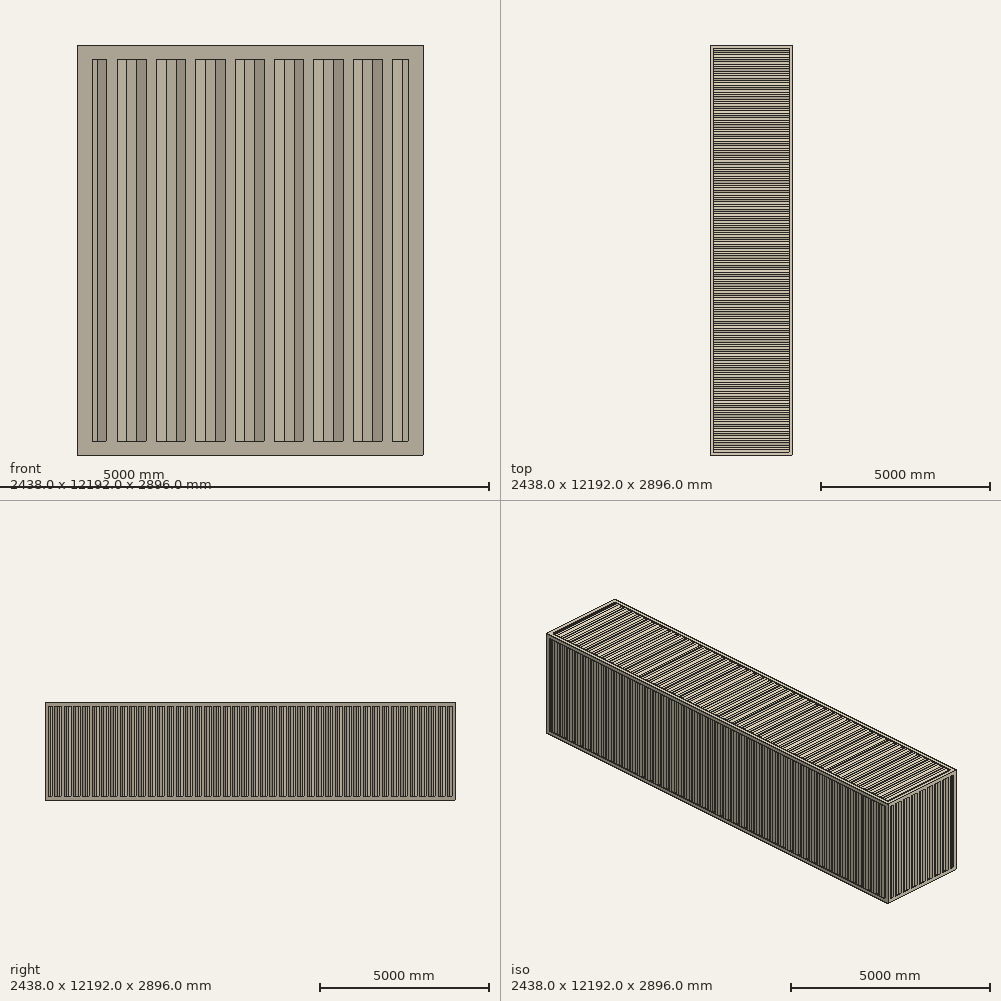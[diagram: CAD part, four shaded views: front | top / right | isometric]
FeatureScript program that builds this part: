
annotation { "Feature Type Name" : "Feature", "Feature Type Description" : "" }
export const myFeature = defineFeature(function(context is Context, id is Id, definition is map)
    precondition{}
    {
        {
            var Q0;
            Q0=qCreatedBy(makeId("Top.planeOp"),FACE);
            var sketch = newSketch(context, id + "F0", { "sketchPlane" : qUnion([Q0])});
            skLineSegment(sketch, "E0.bottom", {"start": v(0, 0) * mm, "end": v(-2438, 0) * mm});
            skLineSegment(sketch, "E0.top", {"start": v(0, 12192) * mm, "end": v(-2438, 12192) * mm});
            skLineSegment(sketch, "E0.left", {"start": v(0, 0) * mm, "end": v(0, 12192) * mm});
            skLineSegment(sketch, "E0.right", {"start": v(-2438, 0) * mm, "end": v(-2438, 12192) * mm});
            skSolve(sketch);
        }
        {
            var Q0;
            Q0=qSketchRegion(id+"F0",true);
            extrude(context, id + "F1", {"entities" : qUnion([Q0]), "depth" : 2896 * mm, "offsetDistance" : 25 * mm});
        }
        {
            var Q0;
            Q0=makeQuery(id+"F1.opExtrude","SWEPT_FACE",FACE,{"disambiguationData":[OSD([sQuery(id+"F0.wireOp",EDGE,"E0.bottom")])]});
            var sketch = newSketch(context, id + "F2", { "sketchPlane" : qUnion([Q0])});
            skLineSegment(sketch, "E1", {"start": v(-2438, 2896) * mm, "end": v(-2338, 2896) * mm});
            skLineSegment(sketch, "E2", {"start": v(-2338, 2896) * mm, "end": v(-2338, 100) * mm});
            skLineSegment(sketch, "E3", {"start": v(-2338, 100) * mm, "end": v(-100, 100) * mm});
            skLineSegment(sketch, "E4", {"start": v(-100, 100) * mm, "end": v(-100, 2796) * mm});
            skLineSegment(sketch, "E5", {"start": v(-100, 2796) * mm, "end": v(-2338, 2796) * mm});
            skSolve(sketch);
        }
        {
            var Q0;
            Q0=qSketchRegion(id+"F2",true);
            extrude(context, id + "F3", {"entities" : qUnion([Q0]), "operationType" : NewBodyOperationType.REMOVE, "oppositeDirection" : true, "depth" : 12192 * mm, "offsetDistance" : 25 * mm});
        }
        {
            var Q0;
            Q0=makeQuery(id+"F1.opExtrude","SWEPT_FACE",FACE,{"disambiguationData":[OSD([sQuery(id+"F0.wireOp",EDGE,"E0.left")])]});
            var sketch = newSketch(context, id + "F4", { "sketchPlane" : qUnion([Q0])});
            skLineSegment(sketch, "E6", {"start": v(0, 2896) * mm, "end": v(100, 2896) * mm});
            skLineSegment(sketch, "E7", {"start": v(100, 2896) * mm, "end": v(100, 100) * mm});
            skLineSegment(sketch, "E8", {"start": v(100, 100) * mm, "end": v(12092, 100) * mm});
            skLineSegment(sketch, "E9", {"start": v(12092, 100) * mm, "end": v(12092, 2796) * mm});
            skLineSegment(sketch, "E10", {"start": v(12092, 2796) * mm, "end": v(100, 2796) * mm});
            skSolve(sketch);
        }
        {
            var Q0;
            Q0=qSketchRegion(id+"F4",true);
            extrude(context, id + "F5", {"entities" : qUnion([Q0]), "operationType" : NewBodyOperationType.REMOVE, "oppositeDirection" : true, "depth" : 2438 * mm, "offsetDistance" : 25 * mm});
        }
        {
            var Q0;
            Q0=makeQuery(id+"F1.opExtrude","CAP_FACE",FACE,{"disambiguationData":[OSD([sQuery(id+"F0.wireOp",EDGE,"E0.bottom"),sQuery(id+"F0.wireOp",EDGE,"E0.top"),sQuery(id+"F0.wireOp",EDGE,"E0.left"),sQuery(id+"F0.wireOp",EDGE,"E0.right")])],"isStart":false});
            var sketch = newSketch(context, id + "F6", { "sketchPlane" : qUnion([Q0])});
            skLineSegment(sketch, "E11", {"start": v(-2438, 0) * mm, "end": v(-2338, 0) * mm});
            skLineSegment(sketch, "E12", {"start": v(-2338, 0) * mm, "end": v(-2338, 12092) * mm});
            skLineSegment(sketch, "E13", {"start": v(-2338, 12092) * mm, "end": v(-100, 12092) * mm});
            skLineSegment(sketch, "E14", {"start": v(-100, 12092) * mm, "end": v(-100, 100) * mm});
            skLineSegment(sketch, "E15", {"start": v(-100, 100) * mm, "end": v(-2338, 100) * mm});
            skSolve(sketch);
        }
        {
            var Q0;
            Q0=qSketchRegion(id+"F6",true);
            extrude(context, id + "F7", {"entities" : qUnion([Q0]), "operationType" : NewBodyOperationType.REMOVE, "oppositeDirection" : true, "depth" : 100 * mm, "offsetDistance" : 25 * mm});
        }
        {
            var Q0;
            Q0=makeQuery(id+"F5.boolean.opBoolean","MERGE",FACE,{"derivedFrom":[makeQuery(id+"F3.boolean.opBoolean","COPY",FACE,{"derivedFrom":makeQuery(id+"F3.opExtrude","SWEPT_FACE",FACE,{"disambiguationData":[OSD([sQuery(id+"F2.wireOp",EDGE,"E3")])]})})],"fromTools":[makeQuery(id+"F5.opExtrude","SWEPT_FACE",FACE,{"disambiguationData":[OSD([sQuery(id+"F4.wireOp",EDGE,"E8")])]})]});
            var sketch = newSketch(context, id + "F8", { "sketchPlane" : qUnion([Q0])});
            skLineSegment(sketch, "E16", {"start": v(-2338, 36) * mm, "end": v(-2301, 36) * mm});
            skLineSegment(sketch, "E17", {"start": v(-2233, 0) * mm, "end": v(-2161, 0) * mm});
            skLineSegment(sketch, "E18", {"start": v(-2093, 36) * mm, "end": v(-2023, 36) * mm});
            skLineSegment(sketch, "E19", {"start": v(-2301, 36) * mm, "end": v(-2233, 0) * mm});
            skLineSegment(sketch, "E20", {"start": v(-2161, 0) * mm, "end": v(-2093, 36) * mm});
            skLineSegment(sketch, "E21.1.0.0", {"start": v(-2023, 36) * mm, "end": v(-1955, 0) * mm});
            skLineSegment(sketch, "E21.1.0.1", {"start": v(-1955, 0) * mm, "end": v(-1883, 0) * mm});
            skLineSegment(sketch, "E21.1.0.2", {"start": v(-1883, 0) * mm, "end": v(-1815, 36) * mm});
            skLineSegment(sketch, "E21.1.0.3", {"start": v(-1815, 36) * mm, "end": v(-1745, 36) * mm});
            skLineSegment(sketch, "E21.2.0.0", {"start": v(-1745, 36) * mm, "end": v(-1677, 0) * mm});
            skLineSegment(sketch, "E21.2.0.1", {"start": v(-1677, 0) * mm, "end": v(-1605, 0) * mm});
            skLineSegment(sketch, "E21.2.0.2", {"start": v(-1605, 0) * mm, "end": v(-1537, 36) * mm});
            skLineSegment(sketch, "E21.2.0.3", {"start": v(-1537, 36) * mm, "end": v(-1467, 36) * mm});
            skLineSegment(sketch, "E21.3.0.0", {"start": v(-1467, 36) * mm, "end": v(-1399, 0) * mm});
            skLineSegment(sketch, "E21.3.0.1", {"start": v(-1399, 0) * mm, "end": v(-1327, 0) * mm});
            skLineSegment(sketch, "E21.3.0.2", {"start": v(-1327, 0) * mm, "end": v(-1259, 36) * mm});
            skLineSegment(sketch, "E21.3.0.3", {"start": v(-1259, 36) * mm, "end": v(-1189, 36) * mm});
            skLineSegment(sketch, "E21.4.0.0", {"start": v(-1189, 36) * mm, "end": v(-1121, 0) * mm});
            skLineSegment(sketch, "E21.4.0.1", {"start": v(-1121, 0) * mm, "end": v(-1049, 0) * mm});
            skLineSegment(sketch, "E21.4.0.2", {"start": v(-1049, 0) * mm, "end": v(-981, 36) * mm});
            skLineSegment(sketch, "E21.4.0.3", {"start": v(-981, 36) * mm, "end": v(-911, 36) * mm});
            skLineSegment(sketch, "E21.5.0.0", {"start": v(-911, 36) * mm, "end": v(-843, 0) * mm});
            skLineSegment(sketch, "E21.5.0.1", {"start": v(-843, 0) * mm, "end": v(-771, 0) * mm});
            skLineSegment(sketch, "E21.5.0.2", {"start": v(-771, 0) * mm, "end": v(-703, 36) * mm});
            skLineSegment(sketch, "E21.5.0.3", {"start": v(-703, 36) * mm, "end": v(-633, 36) * mm});
            skLineSegment(sketch, "E21.6.0.0", {"start": v(-633, 36) * mm, "end": v(-565, 0) * mm});
            skLineSegment(sketch, "E21.6.0.1", {"start": v(-565, 0) * mm, "end": v(-493, 0) * mm});
            skLineSegment(sketch, "E21.6.0.2", {"start": v(-493, 0) * mm, "end": v(-425, 36) * mm});
            skLineSegment(sketch, "E21.6.0.3", {"start": v(-425, 36) * mm, "end": v(-355, 36) * mm});
            skLineSegment(sketch, "E21.direction1", {"start": v(-2301, 36) * mm, "end": v(-2023, 36) * mm, "construction": true});
            skLineSegment(sketch, "E22.1.0.0", {"start": v(-355, 36) * mm, "end": v(-287, 0) * mm});
            skLineSegment(sketch, "E22.1.0.1", {"start": v(-287, 0) * mm, "end": v(-215, 0) * mm});
            skLineSegment(sketch, "E22.1.0.2", {"start": v(-215, 0) * mm, "end": v(-147, 36) * mm});
            skLineSegment(sketch, "E22.direction1", {"start": v(-633, 36) * mm, "end": v(-355, 36) * mm, "construction": true});
            skLineSegment(sketch, "E23", {"start": v(-147, 36) * mm, "end": v(-100, 36) * mm});
            skLineSegment(sketch, "E24.0.1.0", {"start": v(-2301, 37) * mm, "end": v(-2023, 37) * mm, "construction": true});
            skLineSegment(sketch, "E24.0.1.1", {"start": v(-633, 37) * mm, "end": v(-355, 37) * mm, "construction": true});
            skLineSegment(sketch, "E24.0.1.2", {"start": v(-355, 37) * mm, "end": v(-287, 1) * mm});
            skLineSegment(sketch, "E24.0.1.3", {"start": v(-1259, 37) * mm, "end": v(-1189, 37) * mm});
            skLineSegment(sketch, "E24.0.1.4", {"start": v(-147, 37) * mm, "end": v(-100, 37) * mm});
            skLineSegment(sketch, "E24.0.1.5", {"start": v(-1605, 1) * mm, "end": v(-1537, 37) * mm});
            skLineSegment(sketch, "E24.0.1.6", {"start": v(-1467, 37) * mm, "end": v(-1399, 1) * mm});
            skLineSegment(sketch, "E24.0.1.7", {"start": v(-1049, 1) * mm, "end": v(-981, 37) * mm});
            skLineSegment(sketch, "E24.0.1.8", {"start": v(-633, 37) * mm, "end": v(-565, 1) * mm});
            skLineSegment(sketch, "E24.0.1.9", {"start": v(-1955, 1) * mm, "end": v(-1883, 1) * mm});
            skLineSegment(sketch, "E24.0.1.10", {"start": v(-215, 1) * mm, "end": v(-147, 37) * mm});
            skLineSegment(sketch, "E24.0.1.11", {"start": v(-911, 37) * mm, "end": v(-843, 1) * mm});
            skLineSegment(sketch, "E24.0.1.12", {"start": v(-1883, 1) * mm, "end": v(-1815, 37) * mm});
            skLineSegment(sketch, "E24.0.1.13", {"start": v(-2023, 37) * mm, "end": v(-1955, 1) * mm});
            skLineSegment(sketch, "E24.0.1.14", {"start": v(-493, 1) * mm, "end": v(-425, 37) * mm});
            skLineSegment(sketch, "E24.0.1.15", {"start": v(-1677, 1) * mm, "end": v(-1605, 1) * mm});
            skLineSegment(sketch, "E24.0.1.16", {"start": v(-1189, 37) * mm, "end": v(-1121, 1) * mm});
            skLineSegment(sketch, "E24.0.1.17", {"start": v(-1745, 37) * mm, "end": v(-1677, 1) * mm});
            skLineSegment(sketch, "E24.0.1.18", {"start": v(-287, 1) * mm, "end": v(-215, 1) * mm});
            skLineSegment(sketch, "E24.0.1.19", {"start": v(-981, 37) * mm, "end": v(-911, 37) * mm});
            skLineSegment(sketch, "E24.0.1.20", {"start": v(-843, 1) * mm, "end": v(-771, 1) * mm});
            skLineSegment(sketch, "E24.0.1.21", {"start": v(-771, 1) * mm, "end": v(-703, 37) * mm});
            skLineSegment(sketch, "E24.0.1.22", {"start": v(-1815, 37) * mm, "end": v(-1745, 37) * mm});
            skLineSegment(sketch, "E24.0.1.23", {"start": v(-565, 1) * mm, "end": v(-493, 1) * mm});
            skLineSegment(sketch, "E24.0.1.24", {"start": v(-2161, 1) * mm, "end": v(-2093, 37) * mm});
            skLineSegment(sketch, "E24.0.1.25", {"start": v(-1121, 1) * mm, "end": v(-1049, 1) * mm});
            skLineSegment(sketch, "E24.0.1.26", {"start": v(-2301, 37) * mm, "end": v(-2233, 1) * mm});
            skLineSegment(sketch, "E24.0.1.27", {"start": v(-1537, 37) * mm, "end": v(-1467, 37) * mm});
            skLineSegment(sketch, "E24.0.1.28", {"start": v(-1399, 1) * mm, "end": v(-1327, 1) * mm});
            skLineSegment(sketch, "E24.0.1.29", {"start": v(-2233, 1) * mm, "end": v(-2161, 1) * mm});
            skLineSegment(sketch, "E24.0.1.30", {"start": v(-1327, 1) * mm, "end": v(-1259, 37) * mm});
            skLineSegment(sketch, "E24.0.1.31", {"start": v(-425, 37) * mm, "end": v(-355, 37) * mm});
            skLineSegment(sketch, "E24.0.1.32", {"start": v(-2093, 37) * mm, "end": v(-2023, 37) * mm});
            skLineSegment(sketch, "E24.0.1.33", {"start": v(-703, 37) * mm, "end": v(-633, 37) * mm});
            skLineSegment(sketch, "E24.0.1.34", {"start": v(-2338, 37) * mm, "end": v(-2301, 37) * mm});
            skLineSegment(sketch, "E24.direction1", {"start": v(-2338, 36) * mm, "end": v(-2313, 36) * mm, "construction": true});
            skLineSegment(sketch, "E24.direction2", {"start": v(-2338, 36) * mm, "end": v(-2338, 37) * mm, "construction": true});
            skLineSegment(sketch, "E25", {"start": v(-2338, 37) * mm, "end": v(-2338, 36) * mm});
            skLineSegment(sketch, "E26", {"start": v(-100, 37) * mm, "end": v(-100, 36) * mm});
            skSolve(sketch);
        }
        {
            var Q0;
            Q0=qSketchRegion(id+"F8",true);
            extrude(context, id + "F9", {"entities" : qUnion([Q0]), "operationType" : NewBodyOperationType.ADD, "depth" : 2696 * mm, "offsetDistance" : 25 * mm});
        }
        {
            var Q0;
            {var subQ4=makeQuery(id+"F3.boolean.opBoolean","COPY",FACE,{"derivedFrom":makeQuery(id+"F3.opExtrude","SWEPT_FACE",FACE,{"disambiguationData":[OSD([sQuery(id+"F2.wireOp",EDGE,"E3")])]})});var subQ5=makeQuery(id+"F5.opExtrude","SWEPT_FACE",FACE,{"disambiguationData":[OSD([sQuery(id+"F4.wireOp",EDGE,"E8")])]});Q0=makeQuery(id+"F9.boolean.opBoolean","SPLIT",FACE,{"disambiguationData":[TD([makeQuery(id+"F1.opExtrude","SWEPT_FACE",FACE,{"disambiguationData":[OSD([sQuery(id+"F0.wireOp",EDGE,"E0.top")])]})])],"derivedFrom":makeQuery(id+"F5.boolean.opBoolean","MERGE",FACE,{"derivedFrom":[subQ4],"fromTools":[subQ5]})});}
            var sketch = newSketch(context, id + "F10", { "sketchPlane" : qUnion([Q0])});
            skLineSegment(sketch, "E27", {"start": v(-100, 12156) * mm, "end": v(-137, 12156) * mm});
            skLineSegment(sketch, "E28", {"start": v(-205.08, 12191.96) * mm, "end": v(-277.08, 12191.96) * mm});
            skLineSegment(sketch, "E29", {"start": v(-345, 12156) * mm, "end": v(-415, 12156) * mm});
            skLineSegment(sketch, "E30", {"start": v(-137, 12156) * mm, "end": v(-205.08, 12191.96) * mm});
            skLineSegment(sketch, "E31", {"start": v(-277.08, 12191.96) * mm, "end": v(-345, 12156) * mm});
            skLineSegment(sketch, "E32.1.0.0", {"start": v(-415, 12156) * mm, "end": v(-483.08, 12191.96) * mm});
            skLineSegment(sketch, "E32.1.0.1", {"start": v(-483.08, 12191.96) * mm, "end": v(-555.08, 12191.96) * mm});
            skLineSegment(sketch, "E32.1.0.2", {"start": v(-555.08, 12191.96) * mm, "end": v(-623, 12156) * mm});
            skLineSegment(sketch, "E32.1.0.3", {"start": v(-623, 12156) * mm, "end": v(-693, 12156) * mm});
            skLineSegment(sketch, "E32.2.0.0", {"start": v(-693, 12156) * mm, "end": v(-761.08, 12191.96) * mm});
            skLineSegment(sketch, "E32.2.0.1", {"start": v(-761.08, 12191.96) * mm, "end": v(-833.08, 12191.96) * mm});
            skLineSegment(sketch, "E32.2.0.2", {"start": v(-833.08, 12191.96) * mm, "end": v(-901, 12156) * mm});
            skLineSegment(sketch, "E32.2.0.3", {"start": v(-901, 12156) * mm, "end": v(-971, 12156) * mm});
            skLineSegment(sketch, "E32.3.0.0", {"start": v(-971, 12156) * mm, "end": v(-1039.08, 12191.96) * mm});
            skLineSegment(sketch, "E32.3.0.1", {"start": v(-1039.08, 12191.96) * mm, "end": v(-1111.08, 12191.96) * mm});
            skLineSegment(sketch, "E32.3.0.2", {"start": v(-1111.08, 12191.96) * mm, "end": v(-1179, 12156) * mm});
            skLineSegment(sketch, "E32.3.0.3", {"start": v(-1179, 12156) * mm, "end": v(-1249, 12156) * mm});
            skLineSegment(sketch, "E32.4.0.0", {"start": v(-1249, 12156) * mm, "end": v(-1317.08, 12191.96) * mm});
            skLineSegment(sketch, "E32.4.0.1", {"start": v(-1317.08, 12191.96) * mm, "end": v(-1389.08, 12191.96) * mm});
            skLineSegment(sketch, "E32.4.0.2", {"start": v(-1389.08, 12191.96) * mm, "end": v(-1457, 12156) * mm});
            skLineSegment(sketch, "E32.4.0.3", {"start": v(-1457, 12156) * mm, "end": v(-1527, 12156) * mm});
            skLineSegment(sketch, "E32.5.0.0", {"start": v(-1527, 12156) * mm, "end": v(-1595.08, 12191.96) * mm});
            skLineSegment(sketch, "E32.5.0.1", {"start": v(-1595.08, 12191.96) * mm, "end": v(-1667.08, 12191.96) * mm});
            skLineSegment(sketch, "E32.5.0.2", {"start": v(-1667.08, 12191.96) * mm, "end": v(-1735, 12156) * mm});
            skLineSegment(sketch, "E32.5.0.3", {"start": v(-1735, 12156) * mm, "end": v(-1805, 12156) * mm});
            skLineSegment(sketch, "E32.6.0.0", {"start": v(-1805, 12156) * mm, "end": v(-1873.08, 12191.96) * mm});
            skLineSegment(sketch, "E32.6.0.1", {"start": v(-1873.08, 12191.96) * mm, "end": v(-1945.08, 12191.96) * mm});
            skLineSegment(sketch, "E32.6.0.2", {"start": v(-1945.08, 12191.96) * mm, "end": v(-2013, 12156) * mm});
            skLineSegment(sketch, "E32.6.0.3", {"start": v(-2013, 12156) * mm, "end": v(-2083, 12156) * mm});
            skLineSegment(sketch, "E32.direction1", {"start": v(-137, 12156) * mm, "end": v(-415, 12156) * mm, "construction": true});
            skLineSegment(sketch, "E33.1.0.0", {"start": v(-2083, 12156) * mm, "end": v(-2151.08, 12191.96) * mm});
            skLineSegment(sketch, "E33.1.0.1", {"start": v(-2151.08, 12191.96) * mm, "end": v(-2223.08, 12191.96) * mm});
            skLineSegment(sketch, "E33.1.0.2", {"start": v(-2223.08, 12191.96) * mm, "end": v(-2291, 12156) * mm});
            skLineSegment(sketch, "E33.direction1", {"start": v(-1805, 12156) * mm, "end": v(-2083, 12156) * mm, "construction": true});
            skLineSegment(sketch, "E34", {"start": v(-2291, 12156) * mm, "end": v(-2338, 12156) * mm});
            skLineSegment(sketch, "E35.0.1.0", {"start": v(-137, 12155) * mm, "end": v(-415, 12155) * mm, "construction": true});
            skLineSegment(sketch, "E35.0.1.1", {"start": v(-1805, 12155) * mm, "end": v(-2083, 12155) * mm, "construction": true});
            skLineSegment(sketch, "E35.0.1.2", {"start": v(-2083, 12155) * mm, "end": v(-2151.08, 12190.96) * mm});
            skLineSegment(sketch, "E35.0.1.3", {"start": v(-1179, 12155) * mm, "end": v(-1249, 12155) * mm});
            skLineSegment(sketch, "E35.0.1.4", {"start": v(-2291, 12155) * mm, "end": v(-2338, 12155) * mm});
            skLineSegment(sketch, "E35.0.1.5", {"start": v(-833.08, 12190.96) * mm, "end": v(-901, 12155) * mm});
            skLineSegment(sketch, "E35.0.1.6", {"start": v(-971, 12155) * mm, "end": v(-1039.08, 12190.96) * mm});
            skLineSegment(sketch, "E35.0.1.7", {"start": v(-1389.08, 12190.96) * mm, "end": v(-1457, 12155) * mm});
            skLineSegment(sketch, "E35.0.1.8", {"start": v(-1805, 12155) * mm, "end": v(-1873.08, 12190.96) * mm});
            skLineSegment(sketch, "E35.0.1.9", {"start": v(-483.08, 12190.96) * mm, "end": v(-555.08, 12190.96) * mm});
            skLineSegment(sketch, "E35.0.1.10", {"start": v(-2223.08, 12190.96) * mm, "end": v(-2291, 12155) * mm});
            skLineSegment(sketch, "E35.0.1.11", {"start": v(-1527, 12155) * mm, "end": v(-1595.08, 12190.96) * mm});
            skLineSegment(sketch, "E35.0.1.12", {"start": v(-555.08, 12190.96) * mm, "end": v(-623, 12155) * mm});
            skLineSegment(sketch, "E35.0.1.13", {"start": v(-415, 12155) * mm, "end": v(-483.08, 12190.96) * mm});
            skLineSegment(sketch, "E35.0.1.14", {"start": v(-1945.08, 12190.96) * mm, "end": v(-2013, 12155) * mm});
            skLineSegment(sketch, "E35.0.1.15", {"start": v(-761.08, 12190.96) * mm, "end": v(-833.08, 12190.96) * mm});
            skLineSegment(sketch, "E35.0.1.16", {"start": v(-1249, 12155) * mm, "end": v(-1317.08, 12190.96) * mm});
            skLineSegment(sketch, "E35.0.1.17", {"start": v(-693, 12155) * mm, "end": v(-761.08, 12190.96) * mm});
            skLineSegment(sketch, "E35.0.1.18", {"start": v(-2151.08, 12190.96) * mm, "end": v(-2223.08, 12190.96) * mm});
            skLineSegment(sketch, "E35.0.1.19", {"start": v(-1457, 12155) * mm, "end": v(-1527, 12155) * mm});
            skLineSegment(sketch, "E35.0.1.20", {"start": v(-1595.08, 12190.96) * mm, "end": v(-1667.08, 12190.96) * mm});
            skLineSegment(sketch, "E35.0.1.21", {"start": v(-1667.08, 12190.96) * mm, "end": v(-1735, 12155) * mm});
            skLineSegment(sketch, "E35.0.1.22", {"start": v(-623, 12155) * mm, "end": v(-693, 12155) * mm});
            skLineSegment(sketch, "E35.0.1.23", {"start": v(-1873.08, 12190.96) * mm, "end": v(-1945.08, 12190.96) * mm});
            skLineSegment(sketch, "E35.0.1.24", {"start": v(-277.08, 12190.96) * mm, "end": v(-345, 12155) * mm});
            skLineSegment(sketch, "E35.0.1.25", {"start": v(-1317.08, 12190.96) * mm, "end": v(-1389.08, 12190.96) * mm});
            skLineSegment(sketch, "E35.0.1.26", {"start": v(-137, 12155) * mm, "end": v(-205.08, 12190.96) * mm});
            skLineSegment(sketch, "E35.0.1.27", {"start": v(-901, 12155) * mm, "end": v(-971, 12155) * mm});
            skLineSegment(sketch, "E35.0.1.28", {"start": v(-1039.08, 12190.96) * mm, "end": v(-1111.08, 12190.96) * mm});
            skLineSegment(sketch, "E35.0.1.29", {"start": v(-205.08, 12190.96) * mm, "end": v(-277.08, 12190.96) * mm});
            skLineSegment(sketch, "E35.0.1.30", {"start": v(-1111.08, 12190.96) * mm, "end": v(-1179, 12155) * mm});
            skLineSegment(sketch, "E35.0.1.31", {"start": v(-2013, 12155) * mm, "end": v(-2083, 12155) * mm});
            skLineSegment(sketch, "E35.0.1.32", {"start": v(-345, 12155) * mm, "end": v(-415, 12155) * mm});
            skLineSegment(sketch, "E35.0.1.33", {"start": v(-1735, 12155) * mm, "end": v(-1805, 12155) * mm});
            skLineSegment(sketch, "E35.0.1.34", {"start": v(-100, 12155) * mm, "end": v(-137, 12155) * mm});
            skLineSegment(sketch, "E35.direction1", {"start": v(-100, 12156) * mm, "end": v(-125, 12156) * mm, "construction": true});
            skLineSegment(sketch, "E35.direction2", {"start": v(-100, 12156) * mm, "end": v(-100, 12155) * mm, "construction": true});
            skLineSegment(sketch, "E36", {"start": v(-100, 12156) * mm, "end": v(-100, 12155) * mm});
            skLineSegment(sketch, "E37", {"start": v(-2338, 12156) * mm, "end": v(-2338, 12155) * mm});
            skSolve(sketch);
        }
        {
            var Q0;
            Q0=qSketchRegion(id+"F10",true);
            extrude(context, id + "F11", {"entities" : qUnion([Q0]), "operationType" : NewBodyOperationType.ADD, "depth" : 2696 * mm, "offsetDistance" : 25 * mm});
        }
        {
            var Q0;
            {var subQ5=makeQuery(id+"F3.boolean.opBoolean","COPY",FACE,{"derivedFrom":makeQuery(id+"F3.opExtrude","SWEPT_FACE",FACE,{"disambiguationData":[OSD([sQuery(id+"F2.wireOp",EDGE,"E3")])]})});var subQ6=makeQuery(id+"F5.opExtrude","SWEPT_FACE",FACE,{"disambiguationData":[OSD([sQuery(id+"F4.wireOp",EDGE,"E8")])]});var subQ12=makeQuery(id+"F1.opExtrude","SWEPT_FACE",FACE,{"disambiguationData":[OSD([sQuery(id+"F0.wireOp",EDGE,"E0.left")])]});Q0=makeQuery(id+"F11.boolean.opBoolean","SPLIT",FACE,{"disambiguationData":[TD([subQ12])],"derivedFrom":makeQuery(id+"F9.boolean.opBoolean","SPLIT",FACE,{"disambiguationData":[TD([makeQuery(id+"F1.opExtrude","SWEPT_FACE",FACE,{"disambiguationData":[OSD([sQuery(id+"F0.wireOp",EDGE,"E0.top")])]})])],"derivedFrom":makeQuery(id+"F5.boolean.opBoolean","MERGE",FACE,{"derivedFrom":[subQ5],"fromTools":[subQ6]})})});}
            var sketch = newSketch(context, id + "F12", { "sketchPlane" : qUnion([Q0])});
            skLineSegment(sketch, "E38", {"start": v(0, 100) * mm, "end": v(-36, 100) * mm});
            skLineSegment(sketch, "E39", {"start": v(-36, 100.17) * mm, "end": v(-36, 137.17) * mm});
            skLineSegment(sketch, "E40", {"start": v(0, 205.17) * mm, "end": v(0, 277.17) * mm});
            skLineSegment(sketch, "E41", {"start": v(-36, 345.17) * mm, "end": v(-36, 415.17) * mm});
            skLineSegment(sketch, "E42", {"start": v(-36, 137.17) * mm, "end": v(0, 205.17) * mm});
            skLineSegment(sketch, "E43", {"start": v(0, 277.17) * mm, "end": v(-36, 345.17) * mm});
            skLineSegment(sketch, "E44.1.0.0", {"start": v(-36, 415.17) * mm, "end": v(0, 483.17) * mm});
            skLineSegment(sketch, "E44.1.0.1", {"start": v(0, 483.17) * mm, "end": v(0, 555.17) * mm});
            skLineSegment(sketch, "E44.1.0.2", {"start": v(0, 555.17) * mm, "end": v(-36, 623.17) * mm});
            skLineSegment(sketch, "E44.1.0.3", {"start": v(-36, 623.17) * mm, "end": v(-36, 693.17) * mm});
            skLineSegment(sketch, "E44.2.0.0", {"start": v(-36, 693.17) * mm, "end": v(0, 761.17) * mm});
            skLineSegment(sketch, "E44.2.0.1", {"start": v(0, 761.17) * mm, "end": v(0, 833.17) * mm});
            skLineSegment(sketch, "E44.2.0.2", {"start": v(0, 833.17) * mm, "end": v(-36, 901.17) * mm});
            skLineSegment(sketch, "E44.2.0.3", {"start": v(-36, 901.17) * mm, "end": v(-36, 971.17) * mm});
            skLineSegment(sketch, "E44.3.0.0", {"start": v(-36, 971.17) * mm, "end": v(0, 1039.17) * mm});
            skLineSegment(sketch, "E44.3.0.1", {"start": v(0, 1039.17) * mm, "end": v(0, 1111.17) * mm});
            skLineSegment(sketch, "E44.3.0.2", {"start": v(0, 1111.17) * mm, "end": v(-36, 1179.17) * mm});
            skLineSegment(sketch, "E44.3.0.3", {"start": v(-36, 1179.17) * mm, "end": v(-36, 1249.17) * mm});
            skLineSegment(sketch, "E44.4.0.0", {"start": v(-36, 1249.17) * mm, "end": v(0, 1317.17) * mm});
            skLineSegment(sketch, "E44.4.0.1", {"start": v(0, 1317.17) * mm, "end": v(0, 1389.17) * mm});
            skLineSegment(sketch, "E44.4.0.2", {"start": v(0, 1389.17) * mm, "end": v(-36, 1457.17) * mm});
            skLineSegment(sketch, "E44.4.0.3", {"start": v(-36, 1457.17) * mm, "end": v(-36, 1527.17) * mm});
            skLineSegment(sketch, "E44.5.0.0", {"start": v(-36, 1527.17) * mm, "end": v(0, 1595.17) * mm});
            skLineSegment(sketch, "E44.5.0.1", {"start": v(0, 1595.17) * mm, "end": v(0, 1667.17) * mm});
            skLineSegment(sketch, "E44.5.0.2", {"start": v(0, 1667.17) * mm, "end": v(-36, 1735.17) * mm});
            skLineSegment(sketch, "E44.5.0.3", {"start": v(-36, 1735.17) * mm, "end": v(-36, 1805.17) * mm});
            skLineSegment(sketch, "E44.6.0.0", {"start": v(-36, 1805.17) * mm, "end": v(0, 1873.17) * mm});
            skLineSegment(sketch, "E44.6.0.1", {"start": v(0, 1873.17) * mm, "end": v(0, 1945.17) * mm});
            skLineSegment(sketch, "E44.6.0.2", {"start": v(0, 1945.17) * mm, "end": v(-36, 2013.17) * mm});
            skLineSegment(sketch, "E44.6.0.3", {"start": v(-36, 2013.17) * mm, "end": v(-36, 2083.17) * mm});
            skLineSegment(sketch, "E44.direction1", {"start": v(-36, 137.17) * mm, "end": v(-36, 415.17) * mm, "construction": true});
            skLineSegment(sketch, "E45.1.0.0", {"start": v(-36, 2083.17) * mm, "end": v(0, 2151.17) * mm});
            skLineSegment(sketch, "E45.1.0.1", {"start": v(0, 2151.17) * mm, "end": v(0, 2223.17) * mm});
            skLineSegment(sketch, "E45.1.0.2", {"start": v(0, 2223.17) * mm, "end": v(-36, 2291.17) * mm});
            skLineSegment(sketch, "E45.direction1", {"start": v(-36, 1805.17) * mm, "end": v(-36, 2083.17) * mm, "construction": true});
            skLineSegment(sketch, "E46.0.1.0", {"start": v(-37, 137.17) * mm, "end": v(-37, 415.17) * mm, "construction": true});
            skLineSegment(sketch, "E46.0.1.1", {"start": v(-37, 1805.17) * mm, "end": v(-37, 2083.17) * mm, "construction": true});
            skLineSegment(sketch, "E46.0.1.2", {"start": v(-37, 2083.17) * mm, "end": v(-1, 2151.17) * mm});
            skLineSegment(sketch, "E46.0.1.3", {"start": v(-37, 1179.17) * mm, "end": v(-37, 1249.17) * mm});
            skLineSegment(sketch, "E46.0.1.5", {"start": v(-1, 833.17) * mm, "end": v(-37, 901.17) * mm});
            skLineSegment(sketch, "E46.0.1.6", {"start": v(-37, 971.17) * mm, "end": v(-1, 1039.17) * mm});
            skLineSegment(sketch, "E46.0.1.7", {"start": v(-1, 1389.17) * mm, "end": v(-37, 1457.17) * mm});
            skLineSegment(sketch, "E46.0.1.8", {"start": v(-37, 1805.17) * mm, "end": v(-1, 1873.17) * mm});
            skLineSegment(sketch, "E46.0.1.9", {"start": v(-1, 483.17) * mm, "end": v(-1, 555.17) * mm});
            skLineSegment(sketch, "E46.0.1.10", {"start": v(-1, 2223.17) * mm, "end": v(-37, 2291.17) * mm});
            skLineSegment(sketch, "E46.0.1.11", {"start": v(-37, 1527.17) * mm, "end": v(-1, 1595.17) * mm});
            skLineSegment(sketch, "E46.0.1.12", {"start": v(-1, 555.17) * mm, "end": v(-37, 623.17) * mm});
            skLineSegment(sketch, "E46.0.1.13", {"start": v(-37, 415.17) * mm, "end": v(-1, 483.17) * mm});
            skLineSegment(sketch, "E46.0.1.14", {"start": v(-1, 1945.17) * mm, "end": v(-37, 2013.17) * mm});
            skLineSegment(sketch, "E46.0.1.15", {"start": v(-1, 761.17) * mm, "end": v(-1, 833.17) * mm});
            skLineSegment(sketch, "E46.0.1.16", {"start": v(-37, 1249.17) * mm, "end": v(-1, 1317.17) * mm});
            skLineSegment(sketch, "E46.0.1.17", {"start": v(-37, 693.17) * mm, "end": v(-1, 761.17) * mm});
            skLineSegment(sketch, "E46.0.1.18", {"start": v(-1, 2151.17) * mm, "end": v(-1, 2223.17) * mm});
            skLineSegment(sketch, "E46.0.1.19", {"start": v(-37, 1457.17) * mm, "end": v(-37, 1527.17) * mm});
            skLineSegment(sketch, "E46.0.1.20", {"start": v(-1, 1595.17) * mm, "end": v(-1, 1667.17) * mm});
            skLineSegment(sketch, "E46.0.1.21", {"start": v(-1, 1667.17) * mm, "end": v(-37, 1735.17) * mm});
            skLineSegment(sketch, "E46.0.1.22", {"start": v(-37, 623.17) * mm, "end": v(-37, 693.17) * mm});
            skLineSegment(sketch, "E46.0.1.23", {"start": v(-1, 1873.17) * mm, "end": v(-1, 1945.17) * mm});
            skLineSegment(sketch, "E46.0.1.24", {"start": v(-1, 277.17) * mm, "end": v(-37, 345.17) * mm});
            skLineSegment(sketch, "E46.0.1.25", {"start": v(-1, 1317.17) * mm, "end": v(-1, 1389.17) * mm});
            skLineSegment(sketch, "E46.0.1.26", {"start": v(-37, 137.17) * mm, "end": v(-1, 205.17) * mm});
            skLineSegment(sketch, "E46.0.1.27", {"start": v(-37, 901.17) * mm, "end": v(-37, 971.17) * mm});
            skLineSegment(sketch, "E46.0.1.28", {"start": v(-1, 1039.17) * mm, "end": v(-1, 1111.17) * mm});
            skLineSegment(sketch, "E46.0.1.29", {"start": v(-1, 205.17) * mm, "end": v(-1, 277.17) * mm});
            skLineSegment(sketch, "E46.0.1.30", {"start": v(-1, 1111.17) * mm, "end": v(-37, 1179.17) * mm});
            skLineSegment(sketch, "E46.0.1.31", {"start": v(-37, 2013.17) * mm, "end": v(-37, 2083.17) * mm});
            skLineSegment(sketch, "E46.0.1.32", {"start": v(-37, 345.17) * mm, "end": v(-37, 415.17) * mm});
            skLineSegment(sketch, "E46.0.1.33", {"start": v(-37, 1735.17) * mm, "end": v(-37, 1805.17) * mm});
            skLineSegment(sketch, "E46.0.1.34", {"start": v(-37, 100.17) * mm, "end": v(-37, 137.17) * mm});
            skLineSegment(sketch, "E47", {"start": v(-37, 100.17) * mm, "end": v(-37, 100) * mm});
            skLineSegment(sketch, "E48", {"start": v(-37, 100) * mm, "end": v(-36, 100) * mm});
            skLineSegment(sketch, "E49", {"start": v(-36, 100) * mm, "end": v(-36, 100.17) * mm});
            skLineSegment(sketch, "E50.0.1.0", {"start": v(0, 2779.17) * mm, "end": v(-36, 2847.17) * mm});
            skLineSegment(sketch, "E50.0.1.1", {"start": v(-1, 2779.17) * mm, "end": v(-37, 2847.17) * mm});
            skLineSegment(sketch, "E50.0.1.2", {"start": v(0, 2707.17) * mm, "end": v(0, 2779.17) * mm});
            skLineSegment(sketch, "E50.0.1.3", {"start": v(0, 2429.17) * mm, "end": v(0, 2501.17) * mm});
            skLineSegment(sketch, "E50.0.1.4", {"start": v(-37, 2639.17) * mm, "end": v(-1, 2707.17) * mm});
            skLineSegment(sketch, "E50.0.1.5", {"start": v(-37, 2569.17) * mm, "end": v(-37, 2639.17) * mm});
            skLineSegment(sketch, "E50.0.1.6", {"start": v(-37, 2917.17) * mm, "end": v(-1, 2985.17) * mm});
            skLineSegment(sketch, "E50.0.1.7", {"start": v(-1, 2501.17) * mm, "end": v(-37, 2569.17) * mm});
            skLineSegment(sketch, "E50.0.1.8", {"start": v(-36, 2917.17) * mm, "end": v(0, 2985.17) * mm});
            skLineSegment(sketch, "E50.0.1.9", {"start": v(-36, 2569.17) * mm, "end": v(-36, 2639.17) * mm});
            skLineSegment(sketch, "E50.0.1.10", {"start": v(-37, 2291.17) * mm, "end": v(-37, 2361.17) * mm});
            skLineSegment(sketch, "E50.0.1.11", {"start": v(-36, 2847.17) * mm, "end": v(-36, 2917.17) * mm});
            skLineSegment(sketch, "E50.0.1.12", {"start": v(-1, 2707.17) * mm, "end": v(-1, 2779.17) * mm});
            skLineSegment(sketch, "E50.0.1.13", {"start": v(-37, 2361.17) * mm, "end": v(-1, 2429.17) * mm});
            skLineSegment(sketch, "E50.0.1.14", {"start": v(-36, 2361.17) * mm, "end": v(0, 2429.17) * mm});
            skLineSegment(sketch, "E50.0.1.15", {"start": v(0, 2985.17) * mm, "end": v(0, 3057.17) * mm});
            skLineSegment(sketch, "E50.0.1.16", {"start": v(0, 2501.17) * mm, "end": v(-36, 2569.17) * mm});
            skLineSegment(sketch, "E50.0.1.17", {"start": v(-36, 2291.17) * mm, "end": v(-36, 2361.17) * mm});
            skLineSegment(sketch, "E50.0.1.18", {"start": v(-1, 2429.17) * mm, "end": v(-1, 2501.17) * mm});
            skLineSegment(sketch, "E50.0.1.19", {"start": v(-36, 2639.17) * mm, "end": v(0, 2707.17) * mm});
            skLineSegment(sketch, "E50.0.1.20", {"start": v(-1, 2985.17) * mm, "end": v(-1, 3057.17) * mm});
            skLineSegment(sketch, "E50.0.1.21", {"start": v(-37, 2847.17) * mm, "end": v(-37, 2917.17) * mm});
            skLineSegment(sketch, "E50.0.1.22", {"start": v(-36, 3751.17) * mm, "end": v(-36, 4029.17) * mm, "construction": true});
            skLineSegment(sketch, "E50.0.1.23", {"start": v(0, 4169.17) * mm, "end": v(-36, 4237.17) * mm});
            skLineSegment(sketch, "E50.0.1.24", {"start": v(-1, 4169.17) * mm, "end": v(-37, 4237.17) * mm});
            skLineSegment(sketch, "E50.0.1.25", {"start": v(-37, 3751.17) * mm, "end": v(-37, 4029.17) * mm, "construction": true});
            skLineSegment(sketch, "E50.0.1.26", {"start": v(-1, 3335.17) * mm, "end": v(-37, 3403.17) * mm});
            skLineSegment(sketch, "E50.0.1.27", {"start": v(0, 3335.17) * mm, "end": v(-36, 3403.17) * mm});
            skLineSegment(sketch, "E50.0.1.28", {"start": v(0, 4097.17) * mm, "end": v(0, 4169.17) * mm});
            skLineSegment(sketch, "E50.0.1.29", {"start": v(-36, 4029.17) * mm, "end": v(0, 4097.17) * mm});
            skLineSegment(sketch, "E50.0.1.30", {"start": v(0, 3263.17) * mm, "end": v(0, 3335.17) * mm});
            skLineSegment(sketch, "E50.0.1.31", {"start": v(-1, 3263.17) * mm, "end": v(-1, 3335.17) * mm});
            skLineSegment(sketch, "E50.0.1.32", {"start": v(-37, 4029.17) * mm, "end": v(-1, 4097.17) * mm});
            skLineSegment(sketch, "E50.0.1.33", {"start": v(-1, 4097.17) * mm, "end": v(-1, 4169.17) * mm});
            skLineSegment(sketch, "E50.0.1.34", {"start": v(-37, 3681.17) * mm, "end": v(-37, 3751.17) * mm});
            skLineSegment(sketch, "E50.0.1.35", {"start": v(-1, 3541.17) * mm, "end": v(-1, 3613.17) * mm});
            skLineSegment(sketch, "E50.0.1.36", {"start": v(-37, 3125.17) * mm, "end": v(-37, 3195.17) * mm});
            skLineSegment(sketch, "E50.0.1.37", {"start": v(-1, 3891.17) * mm, "end": v(-37, 3959.17) * mm});
            skLineSegment(sketch, "E50.0.1.38", {"start": v(-36, 3473.17) * mm, "end": v(0, 3541.17) * mm});
            skLineSegment(sketch, "E50.0.1.39", {"start": v(-1, 3613.17) * mm, "end": v(-37, 3681.17) * mm});
            skLineSegment(sketch, "E50.0.1.40", {"start": v(0, 3819.17) * mm, "end": v(0, 3891.17) * mm});
            skLineSegment(sketch, "E50.0.1.41", {"start": v(-36, 3751.17) * mm, "end": v(0, 3819.17) * mm});
            skLineSegment(sketch, "E50.0.1.42", {"start": v(0, 3541.17) * mm, "end": v(0, 3613.17) * mm});
            skLineSegment(sketch, "E50.0.1.43", {"start": v(-36, 3125.17) * mm, "end": v(-36, 3195.17) * mm});
            skLineSegment(sketch, "E50.0.1.44", {"start": v(-37, 3473.17) * mm, "end": v(-1, 3541.17) * mm});
            skLineSegment(sketch, "E50.0.1.45", {"start": v(-37, 3195.17) * mm, "end": v(-1, 3263.17) * mm});
            skLineSegment(sketch, "E50.0.1.46", {"start": v(-1, 3057.17) * mm, "end": v(-37, 3125.17) * mm});
            skLineSegment(sketch, "E50.0.1.47", {"start": v(-1, 3819.17) * mm, "end": v(-1, 3891.17) * mm});
            skLineSegment(sketch, "E50.0.1.48", {"start": v(-37, 3403.17) * mm, "end": v(-37, 3473.17) * mm});
            skLineSegment(sketch, "E50.0.1.49", {"start": v(-37, 3959.17) * mm, "end": v(-37, 4029.17) * mm});
            skLineSegment(sketch, "E50.0.1.50", {"start": v(-36, 3403.17) * mm, "end": v(-36, 3473.17) * mm});
            skLineSegment(sketch, "E50.0.1.51", {"start": v(0, 3057.17) * mm, "end": v(-36, 3125.17) * mm});
            skLineSegment(sketch, "E50.0.1.52", {"start": v(-36, 3195.17) * mm, "end": v(0, 3263.17) * mm});
            skLineSegment(sketch, "E50.0.1.53", {"start": v(-36, 3959.17) * mm, "end": v(-36, 4029.17) * mm});
            skLineSegment(sketch, "E50.0.1.54", {"start": v(-36, 3681.17) * mm, "end": v(-36, 3751.17) * mm});
            skLineSegment(sketch, "E50.0.1.55", {"start": v(0, 3891.17) * mm, "end": v(-36, 3959.17) * mm});
            skLineSegment(sketch, "E50.0.1.56", {"start": v(0, 3613.17) * mm, "end": v(-36, 3681.17) * mm});
            skLineSegment(sketch, "E50.0.1.57", {"start": v(-37, 3751.17) * mm, "end": v(-1, 3819.17) * mm});
            skLineSegment(sketch, "E50.0.2.0", {"start": v(0, 4725.17) * mm, "end": v(-36, 4793.17) * mm});
            skLineSegment(sketch, "E50.0.2.1", {"start": v(-1, 4725.17) * mm, "end": v(-37, 4793.17) * mm});
            skLineSegment(sketch, "E50.0.2.2", {"start": v(0, 4653.17) * mm, "end": v(0, 4725.17) * mm});
            skLineSegment(sketch, "E50.0.2.3", {"start": v(0, 4375.17) * mm, "end": v(0, 4447.17) * mm});
            skLineSegment(sketch, "E50.0.2.4", {"start": v(-37, 4585.17) * mm, "end": v(-1, 4653.17) * mm});
            skLineSegment(sketch, "E50.0.2.5", {"start": v(-37, 4515.17) * mm, "end": v(-37, 4585.17) * mm});
            skLineSegment(sketch, "E50.0.2.6", {"start": v(-37, 4863.17) * mm, "end": v(-1, 4931.17) * mm});
            skLineSegment(sketch, "E50.0.2.7", {"start": v(-1, 4447.17) * mm, "end": v(-37, 4515.17) * mm});
            skLineSegment(sketch, "E50.0.2.8", {"start": v(-36, 4863.17) * mm, "end": v(0, 4931.17) * mm});
            skLineSegment(sketch, "E50.0.2.9", {"start": v(-36, 4515.17) * mm, "end": v(-36, 4585.17) * mm});
            skLineSegment(sketch, "E50.0.2.10", {"start": v(-37, 4237.17) * mm, "end": v(-37, 4307.17) * mm});
            skLineSegment(sketch, "E50.0.2.11", {"start": v(-36, 4793.17) * mm, "end": v(-36, 4863.17) * mm});
            skLineSegment(sketch, "E50.0.2.12", {"start": v(-1, 4653.17) * mm, "end": v(-1, 4725.17) * mm});
            skLineSegment(sketch, "E50.0.2.13", {"start": v(-37, 4307.17) * mm, "end": v(-1, 4375.17) * mm});
            skLineSegment(sketch, "E50.0.2.14", {"start": v(-36, 4307.17) * mm, "end": v(0, 4375.17) * mm});
            skLineSegment(sketch, "E50.0.2.15", {"start": v(0, 4931.17) * mm, "end": v(0, 5003.17) * mm});
            skLineSegment(sketch, "E50.0.2.16", {"start": v(0, 4447.17) * mm, "end": v(-36, 4515.17) * mm});
            skLineSegment(sketch, "E50.0.2.17", {"start": v(-36, 4237.17) * mm, "end": v(-36, 4307.17) * mm});
            skLineSegment(sketch, "E50.0.2.18", {"start": v(-1, 4375.17) * mm, "end": v(-1, 4447.17) * mm});
            skLineSegment(sketch, "E50.0.2.19", {"start": v(-36, 4585.17) * mm, "end": v(0, 4653.17) * mm});
            skLineSegment(sketch, "E50.0.2.20", {"start": v(-1, 4931.17) * mm, "end": v(-1, 5003.17) * mm});
            skLineSegment(sketch, "E50.0.2.21", {"start": v(-37, 4793.17) * mm, "end": v(-37, 4863.17) * mm});
            skLineSegment(sketch, "E50.0.2.22", {"start": v(-36, 5697.17) * mm, "end": v(-36, 5975.17) * mm, "construction": true});
            skLineSegment(sketch, "E50.0.2.23", {"start": v(0, 6115.17) * mm, "end": v(-36, 6183.17) * mm});
            skLineSegment(sketch, "E50.0.2.24", {"start": v(-1, 6115.17) * mm, "end": v(-37, 6183.17) * mm});
            skLineSegment(sketch, "E50.0.2.25", {"start": v(-37, 5697.17) * mm, "end": v(-37, 5975.17) * mm, "construction": true});
            skLineSegment(sketch, "E50.0.2.26", {"start": v(-1, 5281.17) * mm, "end": v(-37, 5349.17) * mm});
            skLineSegment(sketch, "E50.0.2.27", {"start": v(0, 5281.17) * mm, "end": v(-36, 5349.17) * mm});
            skLineSegment(sketch, "E50.0.2.28", {"start": v(0, 6043.17) * mm, "end": v(0, 6115.17) * mm});
            skLineSegment(sketch, "E50.0.2.29", {"start": v(-36, 5975.17) * mm, "end": v(0, 6043.17) * mm});
            skLineSegment(sketch, "E50.0.2.30", {"start": v(0, 5209.17) * mm, "end": v(0, 5281.17) * mm});
            skLineSegment(sketch, "E50.0.2.31", {"start": v(-1, 5209.17) * mm, "end": v(-1, 5281.17) * mm});
            skLineSegment(sketch, "E50.0.2.32", {"start": v(-37, 5975.17) * mm, "end": v(-1, 6043.17) * mm});
            skLineSegment(sketch, "E50.0.2.33", {"start": v(-1, 6043.17) * mm, "end": v(-1, 6115.17) * mm});
            skLineSegment(sketch, "E50.0.2.34", {"start": v(-37, 5627.17) * mm, "end": v(-37, 5697.17) * mm});
            skLineSegment(sketch, "E50.0.2.35", {"start": v(-1, 5487.17) * mm, "end": v(-1, 5559.17) * mm});
            skLineSegment(sketch, "E50.0.2.36", {"start": v(-37, 5071.17) * mm, "end": v(-37, 5141.17) * mm});
            skLineSegment(sketch, "E50.0.2.37", {"start": v(-1, 5837.17) * mm, "end": v(-37, 5905.17) * mm});
            skLineSegment(sketch, "E50.0.2.38", {"start": v(-36, 5419.17) * mm, "end": v(0, 5487.17) * mm});
            skLineSegment(sketch, "E50.0.2.39", {"start": v(-1, 5559.17) * mm, "end": v(-37, 5627.17) * mm});
            skLineSegment(sketch, "E50.0.2.40", {"start": v(0, 5765.17) * mm, "end": v(0, 5837.17) * mm});
            skLineSegment(sketch, "E50.0.2.41", {"start": v(-36, 5697.17) * mm, "end": v(0, 5765.17) * mm});
            skLineSegment(sketch, "E50.0.2.42", {"start": v(0, 5487.17) * mm, "end": v(0, 5559.17) * mm});
            skLineSegment(sketch, "E50.0.2.43", {"start": v(-36, 5071.17) * mm, "end": v(-36, 5141.17) * mm});
            skLineSegment(sketch, "E50.0.2.44", {"start": v(-37, 5419.17) * mm, "end": v(-1, 5487.17) * mm});
            skLineSegment(sketch, "E50.0.2.45", {"start": v(-37, 5141.17) * mm, "end": v(-1, 5209.17) * mm});
            skLineSegment(sketch, "E50.0.2.46", {"start": v(-1, 5003.17) * mm, "end": v(-37, 5071.17) * mm});
            skLineSegment(sketch, "E50.0.2.47", {"start": v(-1, 5765.17) * mm, "end": v(-1, 5837.17) * mm});
            skLineSegment(sketch, "E50.0.2.48", {"start": v(-37, 5349.17) * mm, "end": v(-37, 5419.17) * mm});
            skLineSegment(sketch, "E50.0.2.49", {"start": v(-37, 5905.17) * mm, "end": v(-37, 5975.17) * mm});
            skLineSegment(sketch, "E50.0.2.50", {"start": v(-36, 5349.17) * mm, "end": v(-36, 5419.17) * mm});
            skLineSegment(sketch, "E50.0.2.51", {"start": v(0, 5003.17) * mm, "end": v(-36, 5071.17) * mm});
            skLineSegment(sketch, "E50.0.2.52", {"start": v(-36, 5141.17) * mm, "end": v(0, 5209.17) * mm});
            skLineSegment(sketch, "E50.0.2.53", {"start": v(-36, 5905.17) * mm, "end": v(-36, 5975.17) * mm});
            skLineSegment(sketch, "E50.0.2.54", {"start": v(-36, 5627.17) * mm, "end": v(-36, 5697.17) * mm});
            skLineSegment(sketch, "E50.0.2.55", {"start": v(0, 5837.17) * mm, "end": v(-36, 5905.17) * mm});
            skLineSegment(sketch, "E50.0.2.56", {"start": v(0, 5559.17) * mm, "end": v(-36, 5627.17) * mm});
            skLineSegment(sketch, "E50.0.2.57", {"start": v(-37, 5697.17) * mm, "end": v(-1, 5765.17) * mm});
            skLineSegment(sketch, "E50.0.3.0", {"start": v(0, 6671.17) * mm, "end": v(-36, 6739.17) * mm});
            skLineSegment(sketch, "E50.0.3.1", {"start": v(-1, 6671.17) * mm, "end": v(-37, 6739.17) * mm});
            skLineSegment(sketch, "E50.0.3.2", {"start": v(0, 6599.17) * mm, "end": v(0, 6671.17) * mm});
            skLineSegment(sketch, "E50.0.3.3", {"start": v(0, 6321.17) * mm, "end": v(0, 6393.17) * mm});
            skLineSegment(sketch, "E50.0.3.4", {"start": v(-37, 6531.17) * mm, "end": v(-1, 6599.17) * mm});
            skLineSegment(sketch, "E50.0.3.5", {"start": v(-37, 6461.17) * mm, "end": v(-37, 6531.17) * mm});
            skLineSegment(sketch, "E50.0.3.6", {"start": v(-37, 6809.17) * mm, "end": v(-1, 6877.17) * mm});
            skLineSegment(sketch, "E50.0.3.7", {"start": v(-1, 6393.17) * mm, "end": v(-37, 6461.17) * mm});
            skLineSegment(sketch, "E50.0.3.8", {"start": v(-36, 6809.17) * mm, "end": v(0, 6877.17) * mm});
            skLineSegment(sketch, "E50.0.3.9", {"start": v(-36, 6461.17) * mm, "end": v(-36, 6531.17) * mm});
            skLineSegment(sketch, "E50.0.3.10", {"start": v(-37, 6183.17) * mm, "end": v(-37, 6253.17) * mm});
            skLineSegment(sketch, "E50.0.3.11", {"start": v(-36, 6739.17) * mm, "end": v(-36, 6809.17) * mm});
            skLineSegment(sketch, "E50.0.3.12", {"start": v(-1, 6599.17) * mm, "end": v(-1, 6671.17) * mm});
            skLineSegment(sketch, "E50.0.3.13", {"start": v(-37, 6253.17) * mm, "end": v(-1, 6321.17) * mm});
            skLineSegment(sketch, "E50.0.3.14", {"start": v(-36, 6253.17) * mm, "end": v(0, 6321.17) * mm});
            skLineSegment(sketch, "E50.0.3.15", {"start": v(0, 6877.17) * mm, "end": v(0, 6949.17) * mm});
            skLineSegment(sketch, "E50.0.3.16", {"start": v(0, 6393.17) * mm, "end": v(-36, 6461.17) * mm});
            skLineSegment(sketch, "E50.0.3.17", {"start": v(-36, 6183.17) * mm, "end": v(-36, 6253.17) * mm});
            skLineSegment(sketch, "E50.0.3.18", {"start": v(-1, 6321.17) * mm, "end": v(-1, 6393.17) * mm});
            skLineSegment(sketch, "E50.0.3.19", {"start": v(-36, 6531.17) * mm, "end": v(0, 6599.17) * mm});
            skLineSegment(sketch, "E50.0.3.20", {"start": v(-1, 6877.17) * mm, "end": v(-1, 6949.17) * mm});
            skLineSegment(sketch, "E50.0.3.21", {"start": v(-37, 6739.17) * mm, "end": v(-37, 6809.17) * mm});
            skLineSegment(sketch, "E50.0.3.22", {"start": v(-36, 7643.17) * mm, "end": v(-36, 7921.17) * mm, "construction": true});
            skLineSegment(sketch, "E50.0.3.23", {"start": v(0, 8061.17) * mm, "end": v(-36, 8129.17) * mm});
            skLineSegment(sketch, "E50.0.3.24", {"start": v(-1, 8061.17) * mm, "end": v(-37, 8129.17) * mm});
            skLineSegment(sketch, "E50.0.3.25", {"start": v(-37, 7643.17) * mm, "end": v(-37, 7921.17) * mm, "construction": true});
            skLineSegment(sketch, "E50.0.3.26", {"start": v(-1, 7227.17) * mm, "end": v(-37, 7295.17) * mm});
            skLineSegment(sketch, "E50.0.3.27", {"start": v(0, 7227.17) * mm, "end": v(-36, 7295.17) * mm});
            skLineSegment(sketch, "E50.0.3.28", {"start": v(0, 7989.17) * mm, "end": v(0, 8061.17) * mm});
            skLineSegment(sketch, "E50.0.3.29", {"start": v(-36, 7921.17) * mm, "end": v(0, 7989.17) * mm});
            skLineSegment(sketch, "E50.0.3.30", {"start": v(0, 7155.17) * mm, "end": v(0, 7227.17) * mm});
            skLineSegment(sketch, "E50.0.3.31", {"start": v(-1, 7155.17) * mm, "end": v(-1, 7227.17) * mm});
            skLineSegment(sketch, "E50.0.3.32", {"start": v(-37, 7921.17) * mm, "end": v(-1, 7989.17) * mm});
            skLineSegment(sketch, "E50.0.3.33", {"start": v(-1, 7989.17) * mm, "end": v(-1, 8061.17) * mm});
            skLineSegment(sketch, "E50.0.3.34", {"start": v(-37, 7573.17) * mm, "end": v(-37, 7643.17) * mm});
            skLineSegment(sketch, "E50.0.3.35", {"start": v(-1, 7433.17) * mm, "end": v(-1, 7505.17) * mm});
            skLineSegment(sketch, "E50.0.3.36", {"start": v(-37, 7017.17) * mm, "end": v(-37, 7087.17) * mm});
            skLineSegment(sketch, "E50.0.3.37", {"start": v(-1, 7783.17) * mm, "end": v(-37, 7851.17) * mm});
            skLineSegment(sketch, "E50.0.3.38", {"start": v(-36, 7365.17) * mm, "end": v(0, 7433.17) * mm});
            skLineSegment(sketch, "E50.0.3.39", {"start": v(-1, 7505.17) * mm, "end": v(-37, 7573.17) * mm});
            skLineSegment(sketch, "E50.0.3.40", {"start": v(0, 7711.17) * mm, "end": v(0, 7783.17) * mm});
            skLineSegment(sketch, "E50.0.3.41", {"start": v(-36, 7643.17) * mm, "end": v(0, 7711.17) * mm});
            skLineSegment(sketch, "E50.0.3.42", {"start": v(0, 7433.17) * mm, "end": v(0, 7505.17) * mm});
            skLineSegment(sketch, "E50.0.3.43", {"start": v(-36, 7017.17) * mm, "end": v(-36, 7087.17) * mm});
            skLineSegment(sketch, "E50.0.3.44", {"start": v(-37, 7365.17) * mm, "end": v(-1, 7433.17) * mm});
            skLineSegment(sketch, "E50.0.3.45", {"start": v(-37, 7087.17) * mm, "end": v(-1, 7155.17) * mm});
            skLineSegment(sketch, "E50.0.3.46", {"start": v(-1, 6949.17) * mm, "end": v(-37, 7017.17) * mm});
            skLineSegment(sketch, "E50.0.3.47", {"start": v(-1, 7711.17) * mm, "end": v(-1, 7783.17) * mm});
            skLineSegment(sketch, "E50.0.3.48", {"start": v(-37, 7295.17) * mm, "end": v(-37, 7365.17) * mm});
            skLineSegment(sketch, "E50.0.3.49", {"start": v(-37, 7851.17) * mm, "end": v(-37, 7921.17) * mm});
            skLineSegment(sketch, "E50.0.3.50", {"start": v(-36, 7295.17) * mm, "end": v(-36, 7365.17) * mm});
            skLineSegment(sketch, "E50.0.3.51", {"start": v(0, 6949.17) * mm, "end": v(-36, 7017.17) * mm});
            skLineSegment(sketch, "E50.0.3.52", {"start": v(-36, 7087.17) * mm, "end": v(0, 7155.17) * mm});
            skLineSegment(sketch, "E50.0.3.53", {"start": v(-36, 7851.17) * mm, "end": v(-36, 7921.17) * mm});
            skLineSegment(sketch, "E50.0.3.54", {"start": v(-36, 7573.17) * mm, "end": v(-36, 7643.17) * mm});
            skLineSegment(sketch, "E50.0.3.55", {"start": v(0, 7783.17) * mm, "end": v(-36, 7851.17) * mm});
            skLineSegment(sketch, "E50.0.3.56", {"start": v(0, 7505.17) * mm, "end": v(-36, 7573.17) * mm});
            skLineSegment(sketch, "E50.0.3.57", {"start": v(-37, 7643.17) * mm, "end": v(-1, 7711.17) * mm});
            skLineSegment(sketch, "E50.0.4.0", {"start": v(0, 8617.17) * mm, "end": v(-36, 8685.17) * mm});
            skLineSegment(sketch, "E50.0.4.1", {"start": v(-1, 8617.17) * mm, "end": v(-37, 8685.17) * mm});
            skLineSegment(sketch, "E50.0.4.2", {"start": v(0, 8545.17) * mm, "end": v(0, 8617.17) * mm});
            skLineSegment(sketch, "E50.0.4.3", {"start": v(0, 8267.17) * mm, "end": v(0, 8339.17) * mm});
            skLineSegment(sketch, "E50.0.4.4", {"start": v(-37, 8477.17) * mm, "end": v(-1, 8545.17) * mm});
            skLineSegment(sketch, "E50.0.4.5", {"start": v(-37, 8407.17) * mm, "end": v(-37, 8477.17) * mm});
            skLineSegment(sketch, "E50.0.4.6", {"start": v(-37, 8755.17) * mm, "end": v(-1, 8823.17) * mm});
            skLineSegment(sketch, "E50.0.4.7", {"start": v(-1, 8339.17) * mm, "end": v(-37, 8407.17) * mm});
            skLineSegment(sketch, "E50.0.4.8", {"start": v(-36, 8755.17) * mm, "end": v(0, 8823.17) * mm});
            skLineSegment(sketch, "E50.0.4.9", {"start": v(-36, 8407.17) * mm, "end": v(-36, 8477.17) * mm});
            skLineSegment(sketch, "E50.0.4.10", {"start": v(-37, 8129.17) * mm, "end": v(-37, 8199.17) * mm});
            skLineSegment(sketch, "E50.0.4.11", {"start": v(-36, 8685.17) * mm, "end": v(-36, 8755.17) * mm});
            skLineSegment(sketch, "E50.0.4.12", {"start": v(-1, 8545.17) * mm, "end": v(-1, 8617.17) * mm});
            skLineSegment(sketch, "E50.0.4.13", {"start": v(-37, 8199.17) * mm, "end": v(-1, 8267.17) * mm});
            skLineSegment(sketch, "E50.0.4.14", {"start": v(-36, 8199.17) * mm, "end": v(0, 8267.17) * mm});
            skLineSegment(sketch, "E50.0.4.15", {"start": v(0, 8823.17) * mm, "end": v(0, 8895.17) * mm});
            skLineSegment(sketch, "E50.0.4.16", {"start": v(0, 8339.17) * mm, "end": v(-36, 8407.17) * mm});
            skLineSegment(sketch, "E50.0.4.17", {"start": v(-36, 8129.17) * mm, "end": v(-36, 8199.17) * mm});
            skLineSegment(sketch, "E50.0.4.18", {"start": v(-1, 8267.17) * mm, "end": v(-1, 8339.17) * mm});
            skLineSegment(sketch, "E50.0.4.19", {"start": v(-36, 8477.17) * mm, "end": v(0, 8545.17) * mm});
            skLineSegment(sketch, "E50.0.4.20", {"start": v(-1, 8823.17) * mm, "end": v(-1, 8895.17) * mm});
            skLineSegment(sketch, "E50.0.4.21", {"start": v(-37, 8685.17) * mm, "end": v(-37, 8755.17) * mm});
            skLineSegment(sketch, "E50.0.4.22", {"start": v(-36, 9589.17) * mm, "end": v(-36, 9867.17) * mm, "construction": true});
            skLineSegment(sketch, "E50.0.4.23", {"start": v(0, 10007.17) * mm, "end": v(-36, 10075.17) * mm});
            skLineSegment(sketch, "E50.0.4.24", {"start": v(-1, 10007.17) * mm, "end": v(-37, 10075.17) * mm});
            skLineSegment(sketch, "E50.0.4.25", {"start": v(-37, 9589.17) * mm, "end": v(-37, 9867.17) * mm, "construction": true});
            skLineSegment(sketch, "E50.0.4.26", {"start": v(-1, 9173.17) * mm, "end": v(-37, 9241.17) * mm});
            skLineSegment(sketch, "E50.0.4.27", {"start": v(0, 9173.17) * mm, "end": v(-36, 9241.17) * mm});
            skLineSegment(sketch, "E50.0.4.28", {"start": v(0, 9935.17) * mm, "end": v(0, 10007.17) * mm});
            skLineSegment(sketch, "E50.0.4.29", {"start": v(-36, 9867.17) * mm, "end": v(0, 9935.17) * mm});
            skLineSegment(sketch, "E50.0.4.30", {"start": v(0, 9101.17) * mm, "end": v(0, 9173.17) * mm});
            skLineSegment(sketch, "E50.0.4.31", {"start": v(-1, 9101.17) * mm, "end": v(-1, 9173.17) * mm});
            skLineSegment(sketch, "E50.0.4.32", {"start": v(-37, 9867.17) * mm, "end": v(-1, 9935.17) * mm});
            skLineSegment(sketch, "E50.0.4.33", {"start": v(-1, 9935.17) * mm, "end": v(-1, 10007.17) * mm});
            skLineSegment(sketch, "E50.0.4.34", {"start": v(-37, 9519.17) * mm, "end": v(-37, 9589.17) * mm});
            skLineSegment(sketch, "E50.0.4.35", {"start": v(-1, 9379.17) * mm, "end": v(-1, 9451.17) * mm});
            skLineSegment(sketch, "E50.0.4.36", {"start": v(-37, 8963.17) * mm, "end": v(-37, 9033.17) * mm});
            skLineSegment(sketch, "E50.0.4.37", {"start": v(-1, 9729.17) * mm, "end": v(-37, 9797.17) * mm});
            skLineSegment(sketch, "E50.0.4.38", {"start": v(-36, 9311.17) * mm, "end": v(0, 9379.17) * mm});
            skLineSegment(sketch, "E50.0.4.39", {"start": v(-1, 9451.17) * mm, "end": v(-37, 9519.17) * mm});
            skLineSegment(sketch, "E50.0.4.40", {"start": v(0, 9657.17) * mm, "end": v(0, 9729.17) * mm});
            skLineSegment(sketch, "E50.0.4.41", {"start": v(-36, 9589.17) * mm, "end": v(0, 9657.17) * mm});
            skLineSegment(sketch, "E50.0.4.42", {"start": v(0, 9379.17) * mm, "end": v(0, 9451.17) * mm});
            skLineSegment(sketch, "E50.0.4.43", {"start": v(-36, 8963.17) * mm, "end": v(-36, 9033.17) * mm});
            skLineSegment(sketch, "E50.0.4.44", {"start": v(-37, 9311.17) * mm, "end": v(-1, 9379.17) * mm});
            skLineSegment(sketch, "E50.0.4.45", {"start": v(-37, 9033.17) * mm, "end": v(-1, 9101.17) * mm});
            skLineSegment(sketch, "E50.0.4.46", {"start": v(-1, 8895.17) * mm, "end": v(-37, 8963.17) * mm});
            skLineSegment(sketch, "E50.0.4.47", {"start": v(-1, 9657.17) * mm, "end": v(-1, 9729.17) * mm});
            skLineSegment(sketch, "E50.0.4.48", {"start": v(-37, 9241.17) * mm, "end": v(-37, 9311.17) * mm});
            skLineSegment(sketch, "E50.0.4.49", {"start": v(-37, 9797.17) * mm, "end": v(-37, 9867.17) * mm});
            skLineSegment(sketch, "E50.0.4.50", {"start": v(-36, 9241.17) * mm, "end": v(-36, 9311.17) * mm});
            skLineSegment(sketch, "E50.0.4.51", {"start": v(0, 8895.17) * mm, "end": v(-36, 8963.17) * mm});
            skLineSegment(sketch, "E50.0.4.52", {"start": v(-36, 9033.17) * mm, "end": v(0, 9101.17) * mm});
            skLineSegment(sketch, "E50.0.4.53", {"start": v(-36, 9797.17) * mm, "end": v(-36, 9867.17) * mm});
            skLineSegment(sketch, "E50.0.4.54", {"start": v(-36, 9519.17) * mm, "end": v(-36, 9589.17) * mm});
            skLineSegment(sketch, "E50.0.4.55", {"start": v(0, 9729.17) * mm, "end": v(-36, 9797.17) * mm});
            skLineSegment(sketch, "E50.0.4.56", {"start": v(0, 9451.17) * mm, "end": v(-36, 9519.17) * mm});
            skLineSegment(sketch, "E50.0.4.57", {"start": v(-37, 9589.17) * mm, "end": v(-1, 9657.17) * mm});
            skLineSegment(sketch, "E50.0.5.0", {"start": v(0, 10563.17) * mm, "end": v(-36, 10631.17) * mm});
            skLineSegment(sketch, "E50.0.5.1", {"start": v(-1, 10563.17) * mm, "end": v(-37, 10631.17) * mm});
            skLineSegment(sketch, "E50.0.5.2", {"start": v(0, 10491.17) * mm, "end": v(0, 10563.17) * mm});
            skLineSegment(sketch, "E50.0.5.3", {"start": v(0, 10213.17) * mm, "end": v(0, 10285.17) * mm});
            skLineSegment(sketch, "E50.0.5.4", {"start": v(-37, 10423.17) * mm, "end": v(-1, 10491.17) * mm});
            skLineSegment(sketch, "E50.0.5.5", {"start": v(-37, 10353.17) * mm, "end": v(-37, 10423.17) * mm});
            skLineSegment(sketch, "E50.0.5.6", {"start": v(-37, 10701.17) * mm, "end": v(-1, 10769.17) * mm});
            skLineSegment(sketch, "E50.0.5.7", {"start": v(-1, 10285.17) * mm, "end": v(-37, 10353.17) * mm});
            skLineSegment(sketch, "E50.0.5.8", {"start": v(-36, 10701.17) * mm, "end": v(0, 10769.17) * mm});
            skLineSegment(sketch, "E50.0.5.9", {"start": v(-36, 10353.17) * mm, "end": v(-36, 10423.17) * mm});
            skLineSegment(sketch, "E50.0.5.10", {"start": v(-37, 10075.17) * mm, "end": v(-37, 10145.17) * mm});
            skLineSegment(sketch, "E50.0.5.11", {"start": v(-36, 10631.17) * mm, "end": v(-36, 10701.17) * mm});
            skLineSegment(sketch, "E50.0.5.12", {"start": v(-1, 10491.17) * mm, "end": v(-1, 10563.17) * mm});
            skLineSegment(sketch, "E50.0.5.13", {"start": v(-37, 10145.17) * mm, "end": v(-1, 10213.17) * mm});
            skLineSegment(sketch, "E50.0.5.14", {"start": v(-36, 10145.17) * mm, "end": v(0, 10213.17) * mm});
            skLineSegment(sketch, "E50.0.5.15", {"start": v(0, 10769.17) * mm, "end": v(0, 10841.17) * mm});
            skLineSegment(sketch, "E50.0.5.16", {"start": v(0, 10285.17) * mm, "end": v(-36, 10353.17) * mm});
            skLineSegment(sketch, "E50.0.5.17", {"start": v(-36, 10075.17) * mm, "end": v(-36, 10145.17) * mm});
            skLineSegment(sketch, "E50.0.5.18", {"start": v(-1, 10213.17) * mm, "end": v(-1, 10285.17) * mm});
            skLineSegment(sketch, "E50.0.5.19", {"start": v(-36, 10423.17) * mm, "end": v(0, 10491.17) * mm});
            skLineSegment(sketch, "E50.0.5.20", {"start": v(-1, 10769.17) * mm, "end": v(-1, 10841.17) * mm});
            skLineSegment(sketch, "E50.0.5.21", {"start": v(-37, 10631.17) * mm, "end": v(-37, 10701.17) * mm});
            skLineSegment(sketch, "E50.0.5.22", {"start": v(-36, 11535.17) * mm, "end": v(-36, 11813.17) * mm, "construction": true});
            skLineSegment(sketch, "E50.0.5.23", {"start": v(0, 11953.17) * mm, "end": v(-36, 12021.17) * mm});
            skLineSegment(sketch, "E50.0.5.24", {"start": v(-1, 11953.17) * mm, "end": v(-37, 12021.17) * mm});
            skLineSegment(sketch, "E50.0.5.25", {"start": v(-37, 11535.17) * mm, "end": v(-37, 11813.17) * mm, "construction": true});
            skLineSegment(sketch, "E50.0.5.26", {"start": v(-1, 11119.17) * mm, "end": v(-37, 11187.17) * mm});
            skLineSegment(sketch, "E50.0.5.27", {"start": v(0, 11119.17) * mm, "end": v(-36, 11187.17) * mm});
            skLineSegment(sketch, "E50.0.5.28", {"start": v(0, 11881.17) * mm, "end": v(0, 11953.17) * mm});
            skLineSegment(sketch, "E50.0.5.29", {"start": v(-36, 11813.17) * mm, "end": v(0, 11881.17) * mm});
            skLineSegment(sketch, "E50.0.5.30", {"start": v(0, 11047.17) * mm, "end": v(0, 11119.17) * mm});
            skLineSegment(sketch, "E50.0.5.31", {"start": v(-1, 11047.17) * mm, "end": v(-1, 11119.17) * mm});
            skLineSegment(sketch, "E50.0.5.32", {"start": v(-37, 11813.17) * mm, "end": v(-1, 11881.17) * mm});
            skLineSegment(sketch, "E50.0.5.33", {"start": v(-1, 11881.17) * mm, "end": v(-1, 11953.17) * mm});
            skLineSegment(sketch, "E50.0.5.34", {"start": v(-37, 11465.17) * mm, "end": v(-37, 11535.17) * mm});
            skLineSegment(sketch, "E50.0.5.35", {"start": v(-1, 11325.17) * mm, "end": v(-1, 11397.17) * mm});
            skLineSegment(sketch, "E50.0.5.36", {"start": v(-37, 10909.17) * mm, "end": v(-37, 10979.17) * mm});
            skLineSegment(sketch, "E50.0.5.37", {"start": v(-1, 11675.17) * mm, "end": v(-37, 11743.17) * mm});
            skLineSegment(sketch, "E50.0.5.38", {"start": v(-36, 11257.17) * mm, "end": v(0, 11325.17) * mm});
            skLineSegment(sketch, "E50.0.5.39", {"start": v(-1, 11397.17) * mm, "end": v(-37, 11465.17) * mm});
            skLineSegment(sketch, "E50.0.5.40", {"start": v(0, 11603.17) * mm, "end": v(0, 11675.17) * mm});
            skLineSegment(sketch, "E50.0.5.41", {"start": v(-36, 11535.17) * mm, "end": v(0, 11603.17) * mm});
            skLineSegment(sketch, "E50.0.5.42", {"start": v(0, 11325.17) * mm, "end": v(0, 11397.17) * mm});
            skLineSegment(sketch, "E50.0.5.43", {"start": v(-36, 10909.17) * mm, "end": v(-36, 10979.17) * mm});
            skLineSegment(sketch, "E50.0.5.44", {"start": v(-37, 11257.17) * mm, "end": v(-1, 11325.17) * mm});
            skLineSegment(sketch, "E50.0.5.45", {"start": v(-37, 10979.17) * mm, "end": v(-1, 11047.17) * mm});
            skLineSegment(sketch, "E50.0.5.46", {"start": v(-1, 10841.17) * mm, "end": v(-37, 10909.17) * mm});
            skLineSegment(sketch, "E50.0.5.47", {"start": v(-1, 11603.17) * mm, "end": v(-1, 11675.17) * mm});
            skLineSegment(sketch, "E50.0.5.48", {"start": v(-37, 11187.17) * mm, "end": v(-37, 11257.17) * mm});
            skLineSegment(sketch, "E50.0.5.49", {"start": v(-37, 11743.17) * mm, "end": v(-37, 11813.17) * mm});
            skLineSegment(sketch, "E50.0.5.50", {"start": v(-36, 11187.17) * mm, "end": v(-36, 11257.17) * mm});
            skLineSegment(sketch, "E50.0.5.51", {"start": v(0, 10841.17) * mm, "end": v(-36, 10909.17) * mm});
            skLineSegment(sketch, "E50.0.5.52", {"start": v(-36, 10979.17) * mm, "end": v(0, 11047.17) * mm});
            skLineSegment(sketch, "E50.0.5.53", {"start": v(-36, 11743.17) * mm, "end": v(-36, 11813.17) * mm});
            skLineSegment(sketch, "E50.0.5.54", {"start": v(-36, 11465.17) * mm, "end": v(-36, 11535.17) * mm});
            skLineSegment(sketch, "E50.0.5.55", {"start": v(0, 11675.17) * mm, "end": v(-36, 11743.17) * mm});
            skLineSegment(sketch, "E50.0.5.56", {"start": v(0, 11397.17) * mm, "end": v(-36, 11465.17) * mm});
            skLineSegment(sketch, "E50.0.5.57", {"start": v(-37, 11535.17) * mm, "end": v(-1, 11603.17) * mm});
            skLineSegment(sketch, "E50.direction1", {"start": v(-37, 345.17) * mm, "end": v(-12, 345.17) * mm, "construction": true});
            skLineSegment(sketch, "E50.direction2", {"start": v(-37, 345.17) * mm, "end": v(-37, 2291.17) * mm, "construction": true});
            skLineSegment(sketch, "E51", {"start": v(-36, 12021.17) * mm, "end": v(-36, 12092) * mm});
            skLineSegment(sketch, "E52", {"start": v(-36, 12092) * mm, "end": v(-37, 12092) * mm});
            skLineSegment(sketch, "E53", {"start": v(-37, 12092) * mm, "end": v(-37, 12021.17) * mm});
            skSolve(sketch);
        }
        {
            var Q0;
            Q0=qSketchRegion(id+"F12",true);
            extrude(context, id + "F13", {"entities" : qUnion([Q0]), "operationType" : NewBodyOperationType.ADD, "depth" : 2696 * mm, "offsetDistance" : 25 * mm});
        }
        {
            var Q0;
            {var subQ20=makeQuery(id+"F1.opExtrude","SWEPT_FACE",FACE,{"disambiguationData":[OSD([sQuery(id+"F0.wireOp",EDGE,"E0.right")])]});var subQ21=makeQuery(id+"F3.boolean.opBoolean","COPY",FACE,{"derivedFrom":makeQuery(id+"F3.opExtrude","SWEPT_FACE",FACE,{"disambiguationData":[OSD([sQuery(id+"F2.wireOp",EDGE,"E3")])]})});var subQ22=makeQuery(id+"F5.opExtrude","SWEPT_FACE",FACE,{"disambiguationData":[OSD([sQuery(id+"F4.wireOp",EDGE,"E8")])]});var subQ29=makeQuery(id+"F1.opExtrude","SWEPT_FACE",FACE,{"disambiguationData":[OSD([sQuery(id+"F0.wireOp",EDGE,"E0.left")])]});Q0=makeQuery(id+"F13.boolean.opBoolean","SPLIT",FACE,{"disambiguationData":[TD([subQ20])],"derivedFrom":makeQuery(id+"F11.boolean.opBoolean","SPLIT",FACE,{"disambiguationData":[TD([subQ29])],"derivedFrom":makeQuery(id+"F9.boolean.opBoolean","SPLIT",FACE,{"disambiguationData":[TD([makeQuery(id+"F1.opExtrude","SWEPT_FACE",FACE,{"disambiguationData":[OSD([sQuery(id+"F0.wireOp",EDGE,"E0.top")])]})])],"derivedFrom":makeQuery(id+"F5.boolean.opBoolean","MERGE",FACE,{"derivedFrom":[subQ21],"fromTools":[subQ22]})})})});}
            var sketch = newSketch(context, id + "F14", { "sketchPlane" : qUnion([Q0])});
            skLineSegment(sketch, "E54", {"start": v(-2402, 12091.83) * mm, "end": v(-2402, 12054.83) * mm});
            skLineSegment(sketch, "E55", {"start": v(-2438, 11986.83) * mm, "end": v(-2438, 11914.83) * mm});
            skLineSegment(sketch, "E56", {"start": v(-2402, 11846.83) * mm, "end": v(-2402, 11776.83) * mm});
            skLineSegment(sketch, "E57", {"start": v(-2402, 12054.83) * mm, "end": v(-2438, 11986.83) * mm});
            skLineSegment(sketch, "E58", {"start": v(-2438, 11914.83) * mm, "end": v(-2402, 11846.83) * mm});
            skLineSegment(sketch, "E59.1.0.0", {"start": v(-2402, 11776.83) * mm, "end": v(-2438, 11708.83) * mm});
            skLineSegment(sketch, "E59.1.0.1", {"start": v(-2438, 11708.83) * mm, "end": v(-2438, 11636.83) * mm});
            skLineSegment(sketch, "E59.1.0.2", {"start": v(-2438, 11636.83) * mm, "end": v(-2402, 11568.83) * mm});
            skLineSegment(sketch, "E59.1.0.3", {"start": v(-2402, 11568.83) * mm, "end": v(-2402, 11498.83) * mm});
            skLineSegment(sketch, "E59.2.0.0", {"start": v(-2402, 11498.83) * mm, "end": v(-2438, 11430.83) * mm});
            skLineSegment(sketch, "E59.2.0.1", {"start": v(-2438, 11430.83) * mm, "end": v(-2438, 11358.83) * mm});
            skLineSegment(sketch, "E59.2.0.2", {"start": v(-2438, 11358.83) * mm, "end": v(-2402, 11290.83) * mm});
            skLineSegment(sketch, "E59.2.0.3", {"start": v(-2402, 11290.83) * mm, "end": v(-2402, 11220.83) * mm});
            skLineSegment(sketch, "E59.3.0.0", {"start": v(-2402, 11220.83) * mm, "end": v(-2438, 11152.83) * mm});
            skLineSegment(sketch, "E59.3.0.1", {"start": v(-2438, 11152.83) * mm, "end": v(-2438, 11080.83) * mm});
            skLineSegment(sketch, "E59.3.0.2", {"start": v(-2438, 11080.83) * mm, "end": v(-2402, 11012.83) * mm});
            skLineSegment(sketch, "E59.3.0.3", {"start": v(-2402, 11012.83) * mm, "end": v(-2402, 10942.83) * mm});
            skLineSegment(sketch, "E59.4.0.0", {"start": v(-2402, 10942.83) * mm, "end": v(-2438, 10874.83) * mm});
            skLineSegment(sketch, "E59.4.0.1", {"start": v(-2438, 10874.83) * mm, "end": v(-2438, 10802.83) * mm});
            skLineSegment(sketch, "E59.4.0.2", {"start": v(-2438, 10802.83) * mm, "end": v(-2402, 10734.83) * mm});
            skLineSegment(sketch, "E59.4.0.3", {"start": v(-2402, 10734.83) * mm, "end": v(-2402, 10664.83) * mm});
            skLineSegment(sketch, "E59.5.0.0", {"start": v(-2402, 10664.83) * mm, "end": v(-2438, 10596.83) * mm});
            skLineSegment(sketch, "E59.5.0.1", {"start": v(-2438, 10596.83) * mm, "end": v(-2438, 10524.83) * mm});
            skLineSegment(sketch, "E59.5.0.2", {"start": v(-2438, 10524.83) * mm, "end": v(-2402, 10456.83) * mm});
            skLineSegment(sketch, "E59.5.0.3", {"start": v(-2402, 10456.83) * mm, "end": v(-2402, 10386.83) * mm});
            skLineSegment(sketch, "E59.6.0.0", {"start": v(-2402, 10386.83) * mm, "end": v(-2438, 10318.83) * mm});
            skLineSegment(sketch, "E59.6.0.1", {"start": v(-2438, 10318.83) * mm, "end": v(-2438, 10246.83) * mm});
            skLineSegment(sketch, "E59.6.0.2", {"start": v(-2438, 10246.83) * mm, "end": v(-2402, 10178.83) * mm});
            skLineSegment(sketch, "E59.6.0.3", {"start": v(-2402, 10178.83) * mm, "end": v(-2402, 10108.83) * mm});
            skLineSegment(sketch, "E59.direction1", {"start": v(-2402, 12054.83) * mm, "end": v(-2402, 11776.83) * mm, "construction": true});
            skLineSegment(sketch, "E60.1.0.0", {"start": v(-2402, 10108.83) * mm, "end": v(-2438, 10040.83) * mm});
            skLineSegment(sketch, "E60.1.0.1", {"start": v(-2438, 10040.83) * mm, "end": v(-2438, 9968.83) * mm});
            skLineSegment(sketch, "E60.1.0.2", {"start": v(-2438, 9968.83) * mm, "end": v(-2402, 9900.83) * mm});
            skLineSegment(sketch, "E60.direction1", {"start": v(-2402, 10386.83) * mm, "end": v(-2402, 10108.83) * mm, "construction": true});
            skLineSegment(sketch, "E61.0.1.0", {"start": v(-2401, 12054.83) * mm, "end": v(-2401, 11776.83) * mm, "construction": true});
            skLineSegment(sketch, "E61.0.1.1", {"start": v(-2401, 10386.83) * mm, "end": v(-2401, 10108.83) * mm, "construction": true});
            skLineSegment(sketch, "E61.0.1.2", {"start": v(-2401, 10108.83) * mm, "end": v(-2437, 10040.83) * mm});
            skLineSegment(sketch, "E61.0.1.3", {"start": v(-2401, 11012.83) * mm, "end": v(-2401, 10942.83) * mm});
            skLineSegment(sketch, "E61.0.1.5", {"start": v(-2437, 11358.83) * mm, "end": v(-2401, 11290.83) * mm});
            skLineSegment(sketch, "E61.0.1.6", {"start": v(-2401, 11220.83) * mm, "end": v(-2437, 11152.83) * mm});
            skLineSegment(sketch, "E61.0.1.7", {"start": v(-2437, 10802.83) * mm, "end": v(-2401, 10734.83) * mm});
            skLineSegment(sketch, "E61.0.1.8", {"start": v(-2401, 10386.83) * mm, "end": v(-2437, 10318.83) * mm});
            skLineSegment(sketch, "E61.0.1.9", {"start": v(-2437, 11708.83) * mm, "end": v(-2437, 11636.83) * mm});
            skLineSegment(sketch, "E61.0.1.10", {"start": v(-2437, 9968.83) * mm, "end": v(-2401, 9900.83) * mm});
            skLineSegment(sketch, "E61.0.1.11", {"start": v(-2401, 10664.83) * mm, "end": v(-2437, 10596.83) * mm});
            skLineSegment(sketch, "E61.0.1.12", {"start": v(-2437, 11636.83) * mm, "end": v(-2401, 11568.83) * mm});
            skLineSegment(sketch, "E61.0.1.13", {"start": v(-2401, 11776.83) * mm, "end": v(-2437, 11708.83) * mm});
            skLineSegment(sketch, "E61.0.1.14", {"start": v(-2437, 10246.83) * mm, "end": v(-2401, 10178.83) * mm});
            skLineSegment(sketch, "E61.0.1.15", {"start": v(-2437, 11430.83) * mm, "end": v(-2437, 11358.83) * mm});
            skLineSegment(sketch, "E61.0.1.16", {"start": v(-2401, 10942.83) * mm, "end": v(-2437, 10874.83) * mm});
            skLineSegment(sketch, "E61.0.1.17", {"start": v(-2401, 11498.83) * mm, "end": v(-2437, 11430.83) * mm});
            skLineSegment(sketch, "E61.0.1.18", {"start": v(-2437, 10040.83) * mm, "end": v(-2437, 9968.83) * mm});
            skLineSegment(sketch, "E61.0.1.19", {"start": v(-2401, 10734.83) * mm, "end": v(-2401, 10664.83) * mm});
            skLineSegment(sketch, "E61.0.1.20", {"start": v(-2437, 10596.83) * mm, "end": v(-2437, 10524.83) * mm});
            skLineSegment(sketch, "E61.0.1.21", {"start": v(-2437, 10524.83) * mm, "end": v(-2401, 10456.83) * mm});
            skLineSegment(sketch, "E61.0.1.22", {"start": v(-2401, 11568.83) * mm, "end": v(-2401, 11498.83) * mm});
            skLineSegment(sketch, "E61.0.1.23", {"start": v(-2437, 10318.83) * mm, "end": v(-2437, 10246.83) * mm});
            skLineSegment(sketch, "E61.0.1.24", {"start": v(-2437, 11914.83) * mm, "end": v(-2401, 11846.83) * mm});
            skLineSegment(sketch, "E61.0.1.25", {"start": v(-2437, 10874.83) * mm, "end": v(-2437, 10802.83) * mm});
            skLineSegment(sketch, "E61.0.1.26", {"start": v(-2401, 12054.83) * mm, "end": v(-2437, 11986.83) * mm});
            skLineSegment(sketch, "E61.0.1.27", {"start": v(-2401, 11290.83) * mm, "end": v(-2401, 11220.83) * mm});
            skLineSegment(sketch, "E61.0.1.28", {"start": v(-2437, 11152.83) * mm, "end": v(-2437, 11080.83) * mm});
            skLineSegment(sketch, "E61.0.1.29", {"start": v(-2437, 11986.83) * mm, "end": v(-2437, 11914.83) * mm});
            skLineSegment(sketch, "E61.0.1.30", {"start": v(-2437, 11080.83) * mm, "end": v(-2401, 11012.83) * mm});
            skLineSegment(sketch, "E61.0.1.31", {"start": v(-2401, 10178.83) * mm, "end": v(-2401, 10108.83) * mm});
            skLineSegment(sketch, "E61.0.1.32", {"start": v(-2401, 11846.83) * mm, "end": v(-2401, 11776.83) * mm});
            skLineSegment(sketch, "E61.0.1.33", {"start": v(-2401, 10456.83) * mm, "end": v(-2401, 10386.83) * mm});
            skLineSegment(sketch, "E61.0.1.34", {"start": v(-2401, 12091.83) * mm, "end": v(-2401, 12054.83) * mm});
            skLineSegment(sketch, "E62", {"start": v(-2401, 12091.83) * mm, "end": v(-2401, 12092) * mm});
            skLineSegment(sketch, "E63", {"start": v(-2401, 12092) * mm, "end": v(-2402, 12092) * mm});
            skLineSegment(sketch, "E64", {"start": v(-2402, 12092) * mm, "end": v(-2402, 12091.83) * mm});
            skLineSegment(sketch, "E65.0.1.0", {"start": v(-2438, 9412.83) * mm, "end": v(-2402, 9344.83) * mm});
            skLineSegment(sketch, "E65.0.1.1", {"start": v(-2437, 9412.83) * mm, "end": v(-2401, 9344.83) * mm});
            skLineSegment(sketch, "E65.0.1.2", {"start": v(-2438, 9484.83) * mm, "end": v(-2438, 9412.83) * mm});
            skLineSegment(sketch, "E65.0.1.3", {"start": v(-2438, 9762.83) * mm, "end": v(-2438, 9690.83) * mm});
            skLineSegment(sketch, "E65.0.1.4", {"start": v(-2401, 9552.83) * mm, "end": v(-2437, 9484.83) * mm});
            skLineSegment(sketch, "E65.0.1.5", {"start": v(-2401, 9622.83) * mm, "end": v(-2401, 9552.83) * mm});
            skLineSegment(sketch, "E65.0.1.6", {"start": v(-2401, 9274.83) * mm, "end": v(-2437, 9206.83) * mm});
            skLineSegment(sketch, "E65.0.1.7", {"start": v(-2437, 9690.83) * mm, "end": v(-2401, 9622.83) * mm});
            skLineSegment(sketch, "E65.0.1.8", {"start": v(-2402, 9274.83) * mm, "end": v(-2438, 9206.83) * mm});
            skLineSegment(sketch, "E65.0.1.9", {"start": v(-2402, 9622.83) * mm, "end": v(-2402, 9552.83) * mm});
            skLineSegment(sketch, "E65.0.1.10", {"start": v(-2401, 9900.83) * mm, "end": v(-2401, 9830.83) * mm});
            skLineSegment(sketch, "E65.0.1.11", {"start": v(-2402, 9344.83) * mm, "end": v(-2402, 9274.83) * mm});
            skLineSegment(sketch, "E65.0.1.12", {"start": v(-2437, 9484.83) * mm, "end": v(-2437, 9412.83) * mm});
            skLineSegment(sketch, "E65.0.1.13", {"start": v(-2401, 9830.83) * mm, "end": v(-2437, 9762.83) * mm});
            skLineSegment(sketch, "E65.0.1.14", {"start": v(-2402, 9830.83) * mm, "end": v(-2438, 9762.83) * mm});
            skLineSegment(sketch, "E65.0.1.15", {"start": v(-2438, 9206.83) * mm, "end": v(-2438, 9134.83) * mm});
            skLineSegment(sketch, "E65.0.1.16", {"start": v(-2438, 9690.83) * mm, "end": v(-2402, 9622.83) * mm});
            skLineSegment(sketch, "E65.0.1.17", {"start": v(-2402, 9900.83) * mm, "end": v(-2402, 9830.83) * mm});
            skLineSegment(sketch, "E65.0.1.18", {"start": v(-2437, 9762.83) * mm, "end": v(-2437, 9690.83) * mm});
            skLineSegment(sketch, "E65.0.1.19", {"start": v(-2402, 9552.83) * mm, "end": v(-2438, 9484.83) * mm});
            skLineSegment(sketch, "E65.0.1.20", {"start": v(-2437, 9206.83) * mm, "end": v(-2437, 9134.83) * mm});
            skLineSegment(sketch, "E65.0.1.21", {"start": v(-2401, 9344.83) * mm, "end": v(-2401, 9274.83) * mm});
            skLineSegment(sketch, "E65.0.1.22", {"start": v(-2402, 8440.83) * mm, "end": v(-2402, 8162.83) * mm, "construction": true});
            skLineSegment(sketch, "E65.0.1.23", {"start": v(-2438, 8022.83) * mm, "end": v(-2402, 7954.83) * mm});
            skLineSegment(sketch, "E65.0.1.24", {"start": v(-2437, 8022.83) * mm, "end": v(-2401, 7954.83) * mm});
            skLineSegment(sketch, "E65.0.1.25", {"start": v(-2401, 8440.83) * mm, "end": v(-2401, 8162.83) * mm, "construction": true});
            skLineSegment(sketch, "E65.0.1.26", {"start": v(-2437, 8856.83) * mm, "end": v(-2401, 8788.83) * mm});
            skLineSegment(sketch, "E65.0.1.27", {"start": v(-2438, 8856.83) * mm, "end": v(-2402, 8788.83) * mm});
            skLineSegment(sketch, "E65.0.1.28", {"start": v(-2438, 8094.83) * mm, "end": v(-2438, 8022.83) * mm});
            skLineSegment(sketch, "E65.0.1.29", {"start": v(-2402, 8162.83) * mm, "end": v(-2438, 8094.83) * mm});
            skLineSegment(sketch, "E65.0.1.30", {"start": v(-2438, 8928.83) * mm, "end": v(-2438, 8856.83) * mm});
            skLineSegment(sketch, "E65.0.1.31", {"start": v(-2437, 8928.83) * mm, "end": v(-2437, 8856.83) * mm});
            skLineSegment(sketch, "E65.0.1.32", {"start": v(-2401, 8162.83) * mm, "end": v(-2437, 8094.83) * mm});
            skLineSegment(sketch, "E65.0.1.33", {"start": v(-2437, 8094.83) * mm, "end": v(-2437, 8022.83) * mm});
            skLineSegment(sketch, "E65.0.1.34", {"start": v(-2401, 8510.83) * mm, "end": v(-2401, 8440.83) * mm});
            skLineSegment(sketch, "E65.0.1.35", {"start": v(-2437, 8650.83) * mm, "end": v(-2437, 8578.83) * mm});
            skLineSegment(sketch, "E65.0.1.36", {"start": v(-2401, 9066.83) * mm, "end": v(-2401, 8996.83) * mm});
            skLineSegment(sketch, "E65.0.1.37", {"start": v(-2437, 8300.83) * mm, "end": v(-2401, 8232.83) * mm});
            skLineSegment(sketch, "E65.0.1.38", {"start": v(-2402, 8718.83) * mm, "end": v(-2438, 8650.83) * mm});
            skLineSegment(sketch, "E65.0.1.39", {"start": v(-2437, 8578.83) * mm, "end": v(-2401, 8510.83) * mm});
            skLineSegment(sketch, "E65.0.1.40", {"start": v(-2438, 8372.83) * mm, "end": v(-2438, 8300.83) * mm});
            skLineSegment(sketch, "E65.0.1.41", {"start": v(-2402, 8440.83) * mm, "end": v(-2438, 8372.83) * mm});
            skLineSegment(sketch, "E65.0.1.42", {"start": v(-2438, 8650.83) * mm, "end": v(-2438, 8578.83) * mm});
            skLineSegment(sketch, "E65.0.1.43", {"start": v(-2402, 9066.83) * mm, "end": v(-2402, 8996.83) * mm});
            skLineSegment(sketch, "E65.0.1.44", {"start": v(-2401, 8718.83) * mm, "end": v(-2437, 8650.83) * mm});
            skLineSegment(sketch, "E65.0.1.45", {"start": v(-2401, 8996.83) * mm, "end": v(-2437, 8928.83) * mm});
            skLineSegment(sketch, "E65.0.1.46", {"start": v(-2437, 9134.83) * mm, "end": v(-2401, 9066.83) * mm});
            skLineSegment(sketch, "E65.0.1.47", {"start": v(-2437, 8372.83) * mm, "end": v(-2437, 8300.83) * mm});
            skLineSegment(sketch, "E65.0.1.48", {"start": v(-2401, 8788.83) * mm, "end": v(-2401, 8718.83) * mm});
            skLineSegment(sketch, "E65.0.1.49", {"start": v(-2401, 8232.83) * mm, "end": v(-2401, 8162.83) * mm});
            skLineSegment(sketch, "E65.0.1.50", {"start": v(-2402, 8788.83) * mm, "end": v(-2402, 8718.83) * mm});
            skLineSegment(sketch, "E65.0.1.51", {"start": v(-2438, 9134.83) * mm, "end": v(-2402, 9066.83) * mm});
            skLineSegment(sketch, "E65.0.1.52", {"start": v(-2402, 8996.83) * mm, "end": v(-2438, 8928.83) * mm});
            skLineSegment(sketch, "E65.0.1.53", {"start": v(-2402, 8232.83) * mm, "end": v(-2402, 8162.83) * mm});
            skLineSegment(sketch, "E65.0.1.54", {"start": v(-2402, 8510.83) * mm, "end": v(-2402, 8440.83) * mm});
            skLineSegment(sketch, "E65.0.1.55", {"start": v(-2438, 8300.83) * mm, "end": v(-2402, 8232.83) * mm});
            skLineSegment(sketch, "E65.0.1.56", {"start": v(-2438, 8578.83) * mm, "end": v(-2402, 8510.83) * mm});
            skLineSegment(sketch, "E65.0.1.57", {"start": v(-2401, 8440.83) * mm, "end": v(-2437, 8372.83) * mm});
            skLineSegment(sketch, "E65.0.2.0", {"start": v(-2438, 7466.83) * mm, "end": v(-2402, 7398.83) * mm});
            skLineSegment(sketch, "E65.0.2.1", {"start": v(-2437, 7466.83) * mm, "end": v(-2401, 7398.83) * mm});
            skLineSegment(sketch, "E65.0.2.2", {"start": v(-2438, 7538.83) * mm, "end": v(-2438, 7466.83) * mm});
            skLineSegment(sketch, "E65.0.2.3", {"start": v(-2438, 7816.83) * mm, "end": v(-2438, 7744.83) * mm});
            skLineSegment(sketch, "E65.0.2.4", {"start": v(-2401, 7606.83) * mm, "end": v(-2437, 7538.83) * mm});
            skLineSegment(sketch, "E65.0.2.5", {"start": v(-2401, 7676.83) * mm, "end": v(-2401, 7606.83) * mm});
            skLineSegment(sketch, "E65.0.2.6", {"start": v(-2401, 7328.83) * mm, "end": v(-2437, 7260.83) * mm});
            skLineSegment(sketch, "E65.0.2.7", {"start": v(-2437, 7744.83) * mm, "end": v(-2401, 7676.83) * mm});
            skLineSegment(sketch, "E65.0.2.8", {"start": v(-2402, 7328.83) * mm, "end": v(-2438, 7260.83) * mm});
            skLineSegment(sketch, "E65.0.2.9", {"start": v(-2402, 7676.83) * mm, "end": v(-2402, 7606.83) * mm});
            skLineSegment(sketch, "E65.0.2.10", {"start": v(-2401, 7954.83) * mm, "end": v(-2401, 7884.83) * mm});
            skLineSegment(sketch, "E65.0.2.11", {"start": v(-2402, 7398.83) * mm, "end": v(-2402, 7328.83) * mm});
            skLineSegment(sketch, "E65.0.2.12", {"start": v(-2437, 7538.83) * mm, "end": v(-2437, 7466.83) * mm});
            skLineSegment(sketch, "E65.0.2.13", {"start": v(-2401, 7884.83) * mm, "end": v(-2437, 7816.83) * mm});
            skLineSegment(sketch, "E65.0.2.14", {"start": v(-2402, 7884.83) * mm, "end": v(-2438, 7816.83) * mm});
            skLineSegment(sketch, "E65.0.2.15", {"start": v(-2438, 7260.83) * mm, "end": v(-2438, 7188.83) * mm});
            skLineSegment(sketch, "E65.0.2.16", {"start": v(-2438, 7744.83) * mm, "end": v(-2402, 7676.83) * mm});
            skLineSegment(sketch, "E65.0.2.17", {"start": v(-2402, 7954.83) * mm, "end": v(-2402, 7884.83) * mm});
            skLineSegment(sketch, "E65.0.2.18", {"start": v(-2437, 7816.83) * mm, "end": v(-2437, 7744.83) * mm});
            skLineSegment(sketch, "E65.0.2.19", {"start": v(-2402, 7606.83) * mm, "end": v(-2438, 7538.83) * mm});
            skLineSegment(sketch, "E65.0.2.20", {"start": v(-2437, 7260.83) * mm, "end": v(-2437, 7188.83) * mm});
            skLineSegment(sketch, "E65.0.2.21", {"start": v(-2401, 7398.83) * mm, "end": v(-2401, 7328.83) * mm});
            skLineSegment(sketch, "E65.0.2.22", {"start": v(-2402, 6494.83) * mm, "end": v(-2402, 6216.83) * mm, "construction": true});
            skLineSegment(sketch, "E65.0.2.23", {"start": v(-2438, 6076.83) * mm, "end": v(-2402, 6008.83) * mm});
            skLineSegment(sketch, "E65.0.2.24", {"start": v(-2437, 6076.83) * mm, "end": v(-2401, 6008.83) * mm});
            skLineSegment(sketch, "E65.0.2.25", {"start": v(-2401, 6494.83) * mm, "end": v(-2401, 6216.83) * mm, "construction": true});
            skLineSegment(sketch, "E65.0.2.26", {"start": v(-2437, 6910.83) * mm, "end": v(-2401, 6842.83) * mm});
            skLineSegment(sketch, "E65.0.2.27", {"start": v(-2438, 6910.83) * mm, "end": v(-2402, 6842.83) * mm});
            skLineSegment(sketch, "E65.0.2.28", {"start": v(-2438, 6148.83) * mm, "end": v(-2438, 6076.83) * mm});
            skLineSegment(sketch, "E65.0.2.29", {"start": v(-2402, 6216.83) * mm, "end": v(-2438, 6148.83) * mm});
            skLineSegment(sketch, "E65.0.2.30", {"start": v(-2438, 6982.83) * mm, "end": v(-2438, 6910.83) * mm});
            skLineSegment(sketch, "E65.0.2.31", {"start": v(-2437, 6982.83) * mm, "end": v(-2437, 6910.83) * mm});
            skLineSegment(sketch, "E65.0.2.32", {"start": v(-2401, 6216.83) * mm, "end": v(-2437, 6148.83) * mm});
            skLineSegment(sketch, "E65.0.2.33", {"start": v(-2437, 6148.83) * mm, "end": v(-2437, 6076.83) * mm});
            skLineSegment(sketch, "E65.0.2.34", {"start": v(-2401, 6564.83) * mm, "end": v(-2401, 6494.83) * mm});
            skLineSegment(sketch, "E65.0.2.35", {"start": v(-2437, 6704.83) * mm, "end": v(-2437, 6632.83) * mm});
            skLineSegment(sketch, "E65.0.2.36", {"start": v(-2401, 7120.83) * mm, "end": v(-2401, 7050.83) * mm});
            skLineSegment(sketch, "E65.0.2.37", {"start": v(-2437, 6354.83) * mm, "end": v(-2401, 6286.83) * mm});
            skLineSegment(sketch, "E65.0.2.38", {"start": v(-2402, 6772.83) * mm, "end": v(-2438, 6704.83) * mm});
            skLineSegment(sketch, "E65.0.2.39", {"start": v(-2437, 6632.83) * mm, "end": v(-2401, 6564.83) * mm});
            skLineSegment(sketch, "E65.0.2.40", {"start": v(-2438, 6426.83) * mm, "end": v(-2438, 6354.83) * mm});
            skLineSegment(sketch, "E65.0.2.41", {"start": v(-2402, 6494.83) * mm, "end": v(-2438, 6426.83) * mm});
            skLineSegment(sketch, "E65.0.2.42", {"start": v(-2438, 6704.83) * mm, "end": v(-2438, 6632.83) * mm});
            skLineSegment(sketch, "E65.0.2.43", {"start": v(-2402, 7120.83) * mm, "end": v(-2402, 7050.83) * mm});
            skLineSegment(sketch, "E65.0.2.44", {"start": v(-2401, 6772.83) * mm, "end": v(-2437, 6704.83) * mm});
            skLineSegment(sketch, "E65.0.2.45", {"start": v(-2401, 7050.83) * mm, "end": v(-2437, 6982.83) * mm});
            skLineSegment(sketch, "E65.0.2.46", {"start": v(-2437, 7188.83) * mm, "end": v(-2401, 7120.83) * mm});
            skLineSegment(sketch, "E65.0.2.47", {"start": v(-2437, 6426.83) * mm, "end": v(-2437, 6354.83) * mm});
            skLineSegment(sketch, "E65.0.2.48", {"start": v(-2401, 6842.83) * mm, "end": v(-2401, 6772.83) * mm});
            skLineSegment(sketch, "E65.0.2.49", {"start": v(-2401, 6286.83) * mm, "end": v(-2401, 6216.83) * mm});
            skLineSegment(sketch, "E65.0.2.50", {"start": v(-2402, 6842.83) * mm, "end": v(-2402, 6772.83) * mm});
            skLineSegment(sketch, "E65.0.2.51", {"start": v(-2438, 7188.83) * mm, "end": v(-2402, 7120.83) * mm});
            skLineSegment(sketch, "E65.0.2.52", {"start": v(-2402, 7050.83) * mm, "end": v(-2438, 6982.83) * mm});
            skLineSegment(sketch, "E65.0.2.53", {"start": v(-2402, 6286.83) * mm, "end": v(-2402, 6216.83) * mm});
            skLineSegment(sketch, "E65.0.2.54", {"start": v(-2402, 6564.83) * mm, "end": v(-2402, 6494.83) * mm});
            skLineSegment(sketch, "E65.0.2.55", {"start": v(-2438, 6354.83) * mm, "end": v(-2402, 6286.83) * mm});
            skLineSegment(sketch, "E65.0.2.56", {"start": v(-2438, 6632.83) * mm, "end": v(-2402, 6564.83) * mm});
            skLineSegment(sketch, "E65.0.2.57", {"start": v(-2401, 6494.83) * mm, "end": v(-2437, 6426.83) * mm});
            skLineSegment(sketch, "E65.0.3.0", {"start": v(-2438, 5520.83) * mm, "end": v(-2402, 5452.83) * mm});
            skLineSegment(sketch, "E65.0.3.1", {"start": v(-2437, 5520.83) * mm, "end": v(-2401, 5452.83) * mm});
            skLineSegment(sketch, "E65.0.3.2", {"start": v(-2438, 5592.83) * mm, "end": v(-2438, 5520.83) * mm});
            skLineSegment(sketch, "E65.0.3.3", {"start": v(-2438, 5870.83) * mm, "end": v(-2438, 5798.83) * mm});
            skLineSegment(sketch, "E65.0.3.4", {"start": v(-2401, 5660.83) * mm, "end": v(-2437, 5592.83) * mm});
            skLineSegment(sketch, "E65.0.3.5", {"start": v(-2401, 5730.83) * mm, "end": v(-2401, 5660.83) * mm});
            skLineSegment(sketch, "E65.0.3.6", {"start": v(-2401, 5382.83) * mm, "end": v(-2437, 5314.83) * mm});
            skLineSegment(sketch, "E65.0.3.7", {"start": v(-2437, 5798.83) * mm, "end": v(-2401, 5730.83) * mm});
            skLineSegment(sketch, "E65.0.3.8", {"start": v(-2402, 5382.83) * mm, "end": v(-2438, 5314.83) * mm});
            skLineSegment(sketch, "E65.0.3.9", {"start": v(-2402, 5730.83) * mm, "end": v(-2402, 5660.83) * mm});
            skLineSegment(sketch, "E65.0.3.10", {"start": v(-2401, 6008.83) * mm, "end": v(-2401, 5938.83) * mm});
            skLineSegment(sketch, "E65.0.3.11", {"start": v(-2402, 5452.83) * mm, "end": v(-2402, 5382.83) * mm});
            skLineSegment(sketch, "E65.0.3.12", {"start": v(-2437, 5592.83) * mm, "end": v(-2437, 5520.83) * mm});
            skLineSegment(sketch, "E65.0.3.13", {"start": v(-2401, 5938.83) * mm, "end": v(-2437, 5870.83) * mm});
            skLineSegment(sketch, "E65.0.3.14", {"start": v(-2402, 5938.83) * mm, "end": v(-2438, 5870.83) * mm});
            skLineSegment(sketch, "E65.0.3.15", {"start": v(-2438, 5314.83) * mm, "end": v(-2438, 5242.83) * mm});
            skLineSegment(sketch, "E65.0.3.16", {"start": v(-2438, 5798.83) * mm, "end": v(-2402, 5730.83) * mm});
            skLineSegment(sketch, "E65.0.3.17", {"start": v(-2402, 6008.83) * mm, "end": v(-2402, 5938.83) * mm});
            skLineSegment(sketch, "E65.0.3.18", {"start": v(-2437, 5870.83) * mm, "end": v(-2437, 5798.83) * mm});
            skLineSegment(sketch, "E65.0.3.19", {"start": v(-2402, 5660.83) * mm, "end": v(-2438, 5592.83) * mm});
            skLineSegment(sketch, "E65.0.3.20", {"start": v(-2437, 5314.83) * mm, "end": v(-2437, 5242.83) * mm});
            skLineSegment(sketch, "E65.0.3.21", {"start": v(-2401, 5452.83) * mm, "end": v(-2401, 5382.83) * mm});
            skLineSegment(sketch, "E65.0.3.22", {"start": v(-2402, 4548.83) * mm, "end": v(-2402, 4270.83) * mm, "construction": true});
            skLineSegment(sketch, "E65.0.3.23", {"start": v(-2438, 4130.83) * mm, "end": v(-2402, 4062.83) * mm});
            skLineSegment(sketch, "E65.0.3.24", {"start": v(-2437, 4130.83) * mm, "end": v(-2401, 4062.83) * mm});
            skLineSegment(sketch, "E65.0.3.25", {"start": v(-2401, 4548.83) * mm, "end": v(-2401, 4270.83) * mm, "construction": true});
            skLineSegment(sketch, "E65.0.3.26", {"start": v(-2437, 4964.83) * mm, "end": v(-2401, 4896.83) * mm});
            skLineSegment(sketch, "E65.0.3.27", {"start": v(-2438, 4964.83) * mm, "end": v(-2402, 4896.83) * mm});
            skLineSegment(sketch, "E65.0.3.28", {"start": v(-2438, 4202.83) * mm, "end": v(-2438, 4130.83) * mm});
            skLineSegment(sketch, "E65.0.3.29", {"start": v(-2402, 4270.83) * mm, "end": v(-2438, 4202.83) * mm});
            skLineSegment(sketch, "E65.0.3.30", {"start": v(-2438, 5036.83) * mm, "end": v(-2438, 4964.83) * mm});
            skLineSegment(sketch, "E65.0.3.31", {"start": v(-2437, 5036.83) * mm, "end": v(-2437, 4964.83) * mm});
            skLineSegment(sketch, "E65.0.3.32", {"start": v(-2401, 4270.83) * mm, "end": v(-2437, 4202.83) * mm});
            skLineSegment(sketch, "E65.0.3.33", {"start": v(-2437, 4202.83) * mm, "end": v(-2437, 4130.83) * mm});
            skLineSegment(sketch, "E65.0.3.34", {"start": v(-2401, 4618.83) * mm, "end": v(-2401, 4548.83) * mm});
            skLineSegment(sketch, "E65.0.3.35", {"start": v(-2437, 4758.83) * mm, "end": v(-2437, 4686.83) * mm});
            skLineSegment(sketch, "E65.0.3.36", {"start": v(-2401, 5174.83) * mm, "end": v(-2401, 5104.83) * mm});
            skLineSegment(sketch, "E65.0.3.37", {"start": v(-2437, 4408.83) * mm, "end": v(-2401, 4340.83) * mm});
            skLineSegment(sketch, "E65.0.3.38", {"start": v(-2402, 4826.83) * mm, "end": v(-2438, 4758.83) * mm});
            skLineSegment(sketch, "E65.0.3.39", {"start": v(-2437, 4686.83) * mm, "end": v(-2401, 4618.83) * mm});
            skLineSegment(sketch, "E65.0.3.40", {"start": v(-2438, 4480.83) * mm, "end": v(-2438, 4408.83) * mm});
            skLineSegment(sketch, "E65.0.3.41", {"start": v(-2402, 4548.83) * mm, "end": v(-2438, 4480.83) * mm});
            skLineSegment(sketch, "E65.0.3.42", {"start": v(-2438, 4758.83) * mm, "end": v(-2438, 4686.83) * mm});
            skLineSegment(sketch, "E65.0.3.43", {"start": v(-2402, 5174.83) * mm, "end": v(-2402, 5104.83) * mm});
            skLineSegment(sketch, "E65.0.3.44", {"start": v(-2401, 4826.83) * mm, "end": v(-2437, 4758.83) * mm});
            skLineSegment(sketch, "E65.0.3.45", {"start": v(-2401, 5104.83) * mm, "end": v(-2437, 5036.83) * mm});
            skLineSegment(sketch, "E65.0.3.46", {"start": v(-2437, 5242.83) * mm, "end": v(-2401, 5174.83) * mm});
            skLineSegment(sketch, "E65.0.3.47", {"start": v(-2437, 4480.83) * mm, "end": v(-2437, 4408.83) * mm});
            skLineSegment(sketch, "E65.0.3.48", {"start": v(-2401, 4896.83) * mm, "end": v(-2401, 4826.83) * mm});
            skLineSegment(sketch, "E65.0.3.49", {"start": v(-2401, 4340.83) * mm, "end": v(-2401, 4270.83) * mm});
            skLineSegment(sketch, "E65.0.3.50", {"start": v(-2402, 4896.83) * mm, "end": v(-2402, 4826.83) * mm});
            skLineSegment(sketch, "E65.0.3.51", {"start": v(-2438, 5242.83) * mm, "end": v(-2402, 5174.83) * mm});
            skLineSegment(sketch, "E65.0.3.52", {"start": v(-2402, 5104.83) * mm, "end": v(-2438, 5036.83) * mm});
            skLineSegment(sketch, "E65.0.3.53", {"start": v(-2402, 4340.83) * mm, "end": v(-2402, 4270.83) * mm});
            skLineSegment(sketch, "E65.0.3.54", {"start": v(-2402, 4618.83) * mm, "end": v(-2402, 4548.83) * mm});
            skLineSegment(sketch, "E65.0.3.55", {"start": v(-2438, 4408.83) * mm, "end": v(-2402, 4340.83) * mm});
            skLineSegment(sketch, "E65.0.3.56", {"start": v(-2438, 4686.83) * mm, "end": v(-2402, 4618.83) * mm});
            skLineSegment(sketch, "E65.0.3.57", {"start": v(-2401, 4548.83) * mm, "end": v(-2437, 4480.83) * mm});
            skLineSegment(sketch, "E65.0.4.0", {"start": v(-2438, 3574.83) * mm, "end": v(-2402, 3506.83) * mm});
            skLineSegment(sketch, "E65.0.4.1", {"start": v(-2437, 3574.83) * mm, "end": v(-2401, 3506.83) * mm});
            skLineSegment(sketch, "E65.0.4.2", {"start": v(-2438, 3646.83) * mm, "end": v(-2438, 3574.83) * mm});
            skLineSegment(sketch, "E65.0.4.3", {"start": v(-2438, 3924.83) * mm, "end": v(-2438, 3852.83) * mm});
            skLineSegment(sketch, "E65.0.4.4", {"start": v(-2401, 3714.83) * mm, "end": v(-2437, 3646.83) * mm});
            skLineSegment(sketch, "E65.0.4.5", {"start": v(-2401, 3784.83) * mm, "end": v(-2401, 3714.83) * mm});
            skLineSegment(sketch, "E65.0.4.6", {"start": v(-2401, 3436.83) * mm, "end": v(-2437, 3368.83) * mm});
            skLineSegment(sketch, "E65.0.4.7", {"start": v(-2437, 3852.83) * mm, "end": v(-2401, 3784.83) * mm});
            skLineSegment(sketch, "E65.0.4.8", {"start": v(-2402, 3436.83) * mm, "end": v(-2438, 3368.83) * mm});
            skLineSegment(sketch, "E65.0.4.9", {"start": v(-2402, 3784.83) * mm, "end": v(-2402, 3714.83) * mm});
            skLineSegment(sketch, "E65.0.4.10", {"start": v(-2401, 4062.83) * mm, "end": v(-2401, 3992.83) * mm});
            skLineSegment(sketch, "E65.0.4.11", {"start": v(-2402, 3506.83) * mm, "end": v(-2402, 3436.83) * mm});
            skLineSegment(sketch, "E65.0.4.12", {"start": v(-2437, 3646.83) * mm, "end": v(-2437, 3574.83) * mm});
            skLineSegment(sketch, "E65.0.4.13", {"start": v(-2401, 3992.83) * mm, "end": v(-2437, 3924.83) * mm});
            skLineSegment(sketch, "E65.0.4.14", {"start": v(-2402, 3992.83) * mm, "end": v(-2438, 3924.83) * mm});
            skLineSegment(sketch, "E65.0.4.15", {"start": v(-2438, 3368.83) * mm, "end": v(-2438, 3296.83) * mm});
            skLineSegment(sketch, "E65.0.4.16", {"start": v(-2438, 3852.83) * mm, "end": v(-2402, 3784.83) * mm});
            skLineSegment(sketch, "E65.0.4.17", {"start": v(-2402, 4062.83) * mm, "end": v(-2402, 3992.83) * mm});
            skLineSegment(sketch, "E65.0.4.18", {"start": v(-2437, 3924.83) * mm, "end": v(-2437, 3852.83) * mm});
            skLineSegment(sketch, "E65.0.4.19", {"start": v(-2402, 3714.83) * mm, "end": v(-2438, 3646.83) * mm});
            skLineSegment(sketch, "E65.0.4.20", {"start": v(-2437, 3368.83) * mm, "end": v(-2437, 3296.83) * mm});
            skLineSegment(sketch, "E65.0.4.21", {"start": v(-2401, 3506.83) * mm, "end": v(-2401, 3436.83) * mm});
            skLineSegment(sketch, "E65.0.4.22", {"start": v(-2402, 2602.83) * mm, "end": v(-2402, 2324.83) * mm, "construction": true});
            skLineSegment(sketch, "E65.0.4.23", {"start": v(-2438, 2184.83) * mm, "end": v(-2402, 2116.83) * mm});
            skLineSegment(sketch, "E65.0.4.24", {"start": v(-2437, 2184.83) * mm, "end": v(-2401, 2116.83) * mm});
            skLineSegment(sketch, "E65.0.4.25", {"start": v(-2401, 2602.83) * mm, "end": v(-2401, 2324.83) * mm, "construction": true});
            skLineSegment(sketch, "E65.0.4.26", {"start": v(-2437, 3018.83) * mm, "end": v(-2401, 2950.83) * mm});
            skLineSegment(sketch, "E65.0.4.27", {"start": v(-2438, 3018.83) * mm, "end": v(-2402, 2950.83) * mm});
            skLineSegment(sketch, "E65.0.4.28", {"start": v(-2438, 2256.83) * mm, "end": v(-2438, 2184.83) * mm});
            skLineSegment(sketch, "E65.0.4.29", {"start": v(-2402, 2324.83) * mm, "end": v(-2438, 2256.83) * mm});
            skLineSegment(sketch, "E65.0.4.30", {"start": v(-2438, 3090.83) * mm, "end": v(-2438, 3018.83) * mm});
            skLineSegment(sketch, "E65.0.4.31", {"start": v(-2437, 3090.83) * mm, "end": v(-2437, 3018.83) * mm});
            skLineSegment(sketch, "E65.0.4.32", {"start": v(-2401, 2324.83) * mm, "end": v(-2437, 2256.83) * mm});
            skLineSegment(sketch, "E65.0.4.33", {"start": v(-2437, 2256.83) * mm, "end": v(-2437, 2184.83) * mm});
            skLineSegment(sketch, "E65.0.4.34", {"start": v(-2401, 2672.83) * mm, "end": v(-2401, 2602.83) * mm});
            skLineSegment(sketch, "E65.0.4.35", {"start": v(-2437, 2812.83) * mm, "end": v(-2437, 2740.83) * mm});
            skLineSegment(sketch, "E65.0.4.36", {"start": v(-2401, 3228.83) * mm, "end": v(-2401, 3158.83) * mm});
            skLineSegment(sketch, "E65.0.4.37", {"start": v(-2437, 2462.83) * mm, "end": v(-2401, 2394.83) * mm});
            skLineSegment(sketch, "E65.0.4.38", {"start": v(-2402, 2880.83) * mm, "end": v(-2438, 2812.83) * mm});
            skLineSegment(sketch, "E65.0.4.39", {"start": v(-2437, 2740.83) * mm, "end": v(-2401, 2672.83) * mm});
            skLineSegment(sketch, "E65.0.4.40", {"start": v(-2438, 2534.83) * mm, "end": v(-2438, 2462.83) * mm});
            skLineSegment(sketch, "E65.0.4.41", {"start": v(-2402, 2602.83) * mm, "end": v(-2438, 2534.83) * mm});
            skLineSegment(sketch, "E65.0.4.42", {"start": v(-2438, 2812.83) * mm, "end": v(-2438, 2740.83) * mm});
            skLineSegment(sketch, "E65.0.4.43", {"start": v(-2402, 3228.83) * mm, "end": v(-2402, 3158.83) * mm});
            skLineSegment(sketch, "E65.0.4.44", {"start": v(-2401, 2880.83) * mm, "end": v(-2437, 2812.83) * mm});
            skLineSegment(sketch, "E65.0.4.45", {"start": v(-2401, 3158.83) * mm, "end": v(-2437, 3090.83) * mm});
            skLineSegment(sketch, "E65.0.4.46", {"start": v(-2437, 3296.83) * mm, "end": v(-2401, 3228.83) * mm});
            skLineSegment(sketch, "E65.0.4.47", {"start": v(-2437, 2534.83) * mm, "end": v(-2437, 2462.83) * mm});
            skLineSegment(sketch, "E65.0.4.48", {"start": v(-2401, 2950.83) * mm, "end": v(-2401, 2880.83) * mm});
            skLineSegment(sketch, "E65.0.4.49", {"start": v(-2401, 2394.83) * mm, "end": v(-2401, 2324.83) * mm});
            skLineSegment(sketch, "E65.0.4.50", {"start": v(-2402, 2950.83) * mm, "end": v(-2402, 2880.83) * mm});
            skLineSegment(sketch, "E65.0.4.51", {"start": v(-2438, 3296.83) * mm, "end": v(-2402, 3228.83) * mm});
            skLineSegment(sketch, "E65.0.4.52", {"start": v(-2402, 3158.83) * mm, "end": v(-2438, 3090.83) * mm});
            skLineSegment(sketch, "E65.0.4.53", {"start": v(-2402, 2394.83) * mm, "end": v(-2402, 2324.83) * mm});
            skLineSegment(sketch, "E65.0.4.54", {"start": v(-2402, 2672.83) * mm, "end": v(-2402, 2602.83) * mm});
            skLineSegment(sketch, "E65.0.4.55", {"start": v(-2438, 2462.83) * mm, "end": v(-2402, 2394.83) * mm});
            skLineSegment(sketch, "E65.0.4.56", {"start": v(-2438, 2740.83) * mm, "end": v(-2402, 2672.83) * mm});
            skLineSegment(sketch, "E65.0.4.57", {"start": v(-2401, 2602.83) * mm, "end": v(-2437, 2534.83) * mm});
            skLineSegment(sketch, "E65.0.5.0", {"start": v(-2438, 1628.83) * mm, "end": v(-2402, 1560.83) * mm});
            skLineSegment(sketch, "E65.0.5.1", {"start": v(-2437, 1628.83) * mm, "end": v(-2401, 1560.83) * mm});
            skLineSegment(sketch, "E65.0.5.2", {"start": v(-2438, 1700.83) * mm, "end": v(-2438, 1628.83) * mm});
            skLineSegment(sketch, "E65.0.5.3", {"start": v(-2438, 1978.83) * mm, "end": v(-2438, 1906.83) * mm});
            skLineSegment(sketch, "E65.0.5.4", {"start": v(-2401, 1768.83) * mm, "end": v(-2437, 1700.83) * mm});
            skLineSegment(sketch, "E65.0.5.5", {"start": v(-2401, 1838.83) * mm, "end": v(-2401, 1768.83) * mm});
            skLineSegment(sketch, "E65.0.5.6", {"start": v(-2401, 1490.83) * mm, "end": v(-2437, 1422.83) * mm});
            skLineSegment(sketch, "E65.0.5.7", {"start": v(-2437, 1906.83) * mm, "end": v(-2401, 1838.83) * mm});
            skLineSegment(sketch, "E65.0.5.8", {"start": v(-2402, 1490.83) * mm, "end": v(-2438, 1422.83) * mm});
            skLineSegment(sketch, "E65.0.5.9", {"start": v(-2402, 1838.83) * mm, "end": v(-2402, 1768.83) * mm});
            skLineSegment(sketch, "E65.0.5.10", {"start": v(-2401, 2116.83) * mm, "end": v(-2401, 2046.83) * mm});
            skLineSegment(sketch, "E65.0.5.11", {"start": v(-2402, 1560.83) * mm, "end": v(-2402, 1490.83) * mm});
            skLineSegment(sketch, "E65.0.5.12", {"start": v(-2437, 1700.83) * mm, "end": v(-2437, 1628.83) * mm});
            skLineSegment(sketch, "E65.0.5.13", {"start": v(-2401, 2046.83) * mm, "end": v(-2437, 1978.83) * mm});
            skLineSegment(sketch, "E65.0.5.14", {"start": v(-2402, 2046.83) * mm, "end": v(-2438, 1978.83) * mm});
            skLineSegment(sketch, "E65.0.5.15", {"start": v(-2438, 1422.83) * mm, "end": v(-2438, 1350.83) * mm});
            skLineSegment(sketch, "E65.0.5.16", {"start": v(-2438, 1906.83) * mm, "end": v(-2402, 1838.83) * mm});
            skLineSegment(sketch, "E65.0.5.17", {"start": v(-2402, 2116.83) * mm, "end": v(-2402, 2046.83) * mm});
            skLineSegment(sketch, "E65.0.5.18", {"start": v(-2437, 1978.83) * mm, "end": v(-2437, 1906.83) * mm});
            skLineSegment(sketch, "E65.0.5.19", {"start": v(-2402, 1768.83) * mm, "end": v(-2438, 1700.83) * mm});
            skLineSegment(sketch, "E65.0.5.20", {"start": v(-2437, 1422.83) * mm, "end": v(-2437, 1350.83) * mm});
            skLineSegment(sketch, "E65.0.5.21", {"start": v(-2401, 1560.83) * mm, "end": v(-2401, 1490.83) * mm});
            skLineSegment(sketch, "E65.0.5.22", {"start": v(-2402, 656.83) * mm, "end": v(-2402, 378.83) * mm, "construction": true});
            skLineSegment(sketch, "E65.0.5.23", {"start": v(-2438, 238.83) * mm, "end": v(-2402, 170.83) * mm});
            skLineSegment(sketch, "E65.0.5.24", {"start": v(-2437, 238.83) * mm, "end": v(-2401, 170.83) * mm});
            skLineSegment(sketch, "E65.0.5.25", {"start": v(-2401, 656.83) * mm, "end": v(-2401, 378.83) * mm, "construction": true});
            skLineSegment(sketch, "E65.0.5.26", {"start": v(-2437, 1072.83) * mm, "end": v(-2401, 1004.83) * mm});
            skLineSegment(sketch, "E65.0.5.27", {"start": v(-2438, 1072.83) * mm, "end": v(-2402, 1004.83) * mm});
            skLineSegment(sketch, "E65.0.5.28", {"start": v(-2438, 310.83) * mm, "end": v(-2438, 238.83) * mm});
            skLineSegment(sketch, "E65.0.5.29", {"start": v(-2402, 378.83) * mm, "end": v(-2438, 310.83) * mm});
            skLineSegment(sketch, "E65.0.5.30", {"start": v(-2438, 1144.83) * mm, "end": v(-2438, 1072.83) * mm});
            skLineSegment(sketch, "E65.0.5.31", {"start": v(-2437, 1144.83) * mm, "end": v(-2437, 1072.83) * mm});
            skLineSegment(sketch, "E65.0.5.32", {"start": v(-2401, 378.83) * mm, "end": v(-2437, 310.83) * mm});
            skLineSegment(sketch, "E65.0.5.33", {"start": v(-2437, 310.83) * mm, "end": v(-2437, 238.83) * mm});
            skLineSegment(sketch, "E65.0.5.34", {"start": v(-2401, 726.83) * mm, "end": v(-2401, 656.83) * mm});
            skLineSegment(sketch, "E65.0.5.35", {"start": v(-2437, 866.83) * mm, "end": v(-2437, 794.83) * mm});
            skLineSegment(sketch, "E65.0.5.36", {"start": v(-2401, 1282.83) * mm, "end": v(-2401, 1212.83) * mm});
            skLineSegment(sketch, "E65.0.5.37", {"start": v(-2437, 516.83) * mm, "end": v(-2401, 448.83) * mm});
            skLineSegment(sketch, "E65.0.5.38", {"start": v(-2402, 934.83) * mm, "end": v(-2438, 866.83) * mm});
            skLineSegment(sketch, "E65.0.5.39", {"start": v(-2437, 794.83) * mm, "end": v(-2401, 726.83) * mm});
            skLineSegment(sketch, "E65.0.5.40", {"start": v(-2438, 588.83) * mm, "end": v(-2438, 516.83) * mm});
            skLineSegment(sketch, "E65.0.5.41", {"start": v(-2402, 656.83) * mm, "end": v(-2438, 588.83) * mm});
            skLineSegment(sketch, "E65.0.5.42", {"start": v(-2438, 866.83) * mm, "end": v(-2438, 794.83) * mm});
            skLineSegment(sketch, "E65.0.5.43", {"start": v(-2402, 1282.83) * mm, "end": v(-2402, 1212.83) * mm});
            skLineSegment(sketch, "E65.0.5.44", {"start": v(-2401, 934.83) * mm, "end": v(-2437, 866.83) * mm});
            skLineSegment(sketch, "E65.0.5.45", {"start": v(-2401, 1212.83) * mm, "end": v(-2437, 1144.83) * mm});
            skLineSegment(sketch, "E65.0.5.46", {"start": v(-2437, 1350.83) * mm, "end": v(-2401, 1282.83) * mm});
            skLineSegment(sketch, "E65.0.5.47", {"start": v(-2437, 588.83) * mm, "end": v(-2437, 516.83) * mm});
            skLineSegment(sketch, "E65.0.5.48", {"start": v(-2401, 1004.83) * mm, "end": v(-2401, 934.83) * mm});
            skLineSegment(sketch, "E65.0.5.49", {"start": v(-2401, 448.83) * mm, "end": v(-2401, 378.83) * mm});
            skLineSegment(sketch, "E65.0.5.50", {"start": v(-2402, 1004.83) * mm, "end": v(-2402, 934.83) * mm});
            skLineSegment(sketch, "E65.0.5.51", {"start": v(-2438, 1350.83) * mm, "end": v(-2402, 1282.83) * mm});
            skLineSegment(sketch, "E65.0.5.52", {"start": v(-2402, 1212.83) * mm, "end": v(-2438, 1144.83) * mm});
            skLineSegment(sketch, "E65.0.5.53", {"start": v(-2402, 448.83) * mm, "end": v(-2402, 378.83) * mm});
            skLineSegment(sketch, "E65.0.5.54", {"start": v(-2402, 726.83) * mm, "end": v(-2402, 656.83) * mm});
            skLineSegment(sketch, "E65.0.5.55", {"start": v(-2438, 516.83) * mm, "end": v(-2402, 448.83) * mm});
            skLineSegment(sketch, "E65.0.5.56", {"start": v(-2438, 794.83) * mm, "end": v(-2402, 726.83) * mm});
            skLineSegment(sketch, "E65.0.5.57", {"start": v(-2401, 656.83) * mm, "end": v(-2437, 588.83) * mm});
            skLineSegment(sketch, "E65.direction1", {"start": v(-2401, 11846.83) * mm, "end": v(-2426, 11846.83) * mm, "construction": true});
            skLineSegment(sketch, "E65.direction2", {"start": v(-2401, 11846.83) * mm, "end": v(-2401, 9900.83) * mm, "construction": true});
            skLineSegment(sketch, "E66", {"start": v(-2402, 170.83) * mm, "end": v(-2402, 100) * mm});
            skLineSegment(sketch, "E67", {"start": v(-2402, 100) * mm, "end": v(-2401, 100) * mm});
            skLineSegment(sketch, "E68", {"start": v(-2401, 100) * mm, "end": v(-2401, 170.83) * mm});
            skSolve(sketch);
        }
        {
            var Q0;
            Q0=qSketchRegion(id+"F14",true);
            extrude(context, id + "F15", {"entities" : qUnion([Q0]), "operationType" : NewBodyOperationType.ADD, "depth" : 2696 * mm, "offsetDistance" : 25 * mm});
        }
        {
            var Q0;
            Q0=makeQuery(id+"F7.boolean.opBoolean","COPY",FACE,{"derivedFrom":makeQuery(id+"F7.opExtrude","SWEPT_FACE",FACE,{"disambiguationData":[OSD([sQuery(id+"F6.wireOp",EDGE,"E12")])]})});
            var sketch = newSketch(context, id + "F16", { "sketchPlane" : qUnion([Q0])});
            skLineSegment(sketch, "E69", {"start": v(12091.83, 2859.97) * mm, "end": v(12054.83, 2859.97) * mm});
            skLineSegment(sketch, "E70", {"start": v(11986.83, 2895.97) * mm, "end": v(11914.83, 2895.97) * mm});
            skLineSegment(sketch, "E71", {"start": v(11846.83, 2859.97) * mm, "end": v(11776.83, 2859.97) * mm});
            skLineSegment(sketch, "E72", {"start": v(12054.83, 2859.97) * mm, "end": v(11986.83, 2895.97) * mm});
            skLineSegment(sketch, "E73", {"start": v(11914.83, 2895.97) * mm, "end": v(11846.83, 2859.97) * mm});
            skLineSegment(sketch, "E74.1.0.0", {"start": v(11776.83, 2859.97) * mm, "end": v(11708.83, 2895.97) * mm});
            skLineSegment(sketch, "E74.1.0.1", {"start": v(11708.83, 2895.97) * mm, "end": v(11636.83, 2895.97) * mm});
            skLineSegment(sketch, "E74.1.0.2", {"start": v(11636.83, 2895.97) * mm, "end": v(11568.83, 2859.97) * mm});
            skLineSegment(sketch, "E74.1.0.3", {"start": v(11568.83, 2859.97) * mm, "end": v(11498.83, 2859.97) * mm});
            skLineSegment(sketch, "E74.2.0.0", {"start": v(11498.83, 2859.97) * mm, "end": v(11430.83, 2895.97) * mm});
            skLineSegment(sketch, "E74.2.0.1", {"start": v(11430.83, 2895.97) * mm, "end": v(11358.83, 2895.97) * mm});
            skLineSegment(sketch, "E74.2.0.2", {"start": v(11358.83, 2895.97) * mm, "end": v(11290.83, 2859.97) * mm});
            skLineSegment(sketch, "E74.2.0.3", {"start": v(11290.83, 2859.97) * mm, "end": v(11220.83, 2859.97) * mm});
            skLineSegment(sketch, "E74.3.0.0", {"start": v(11220.83, 2859.97) * mm, "end": v(11152.83, 2895.97) * mm});
            skLineSegment(sketch, "E74.3.0.1", {"start": v(11152.83, 2895.97) * mm, "end": v(11080.83, 2895.97) * mm});
            skLineSegment(sketch, "E74.3.0.2", {"start": v(11080.83, 2895.97) * mm, "end": v(11012.83, 2859.97) * mm});
            skLineSegment(sketch, "E74.3.0.3", {"start": v(11012.83, 2859.97) * mm, "end": v(10942.83, 2859.97) * mm});
            skLineSegment(sketch, "E74.4.0.0", {"start": v(10942.83, 2859.97) * mm, "end": v(10874.83, 2895.97) * mm});
            skLineSegment(sketch, "E74.4.0.1", {"start": v(10874.83, 2895.97) * mm, "end": v(10802.83, 2895.97) * mm});
            skLineSegment(sketch, "E74.4.0.2", {"start": v(10802.83, 2895.97) * mm, "end": v(10734.83, 2859.97) * mm});
            skLineSegment(sketch, "E74.4.0.3", {"start": v(10734.83, 2859.97) * mm, "end": v(10664.83, 2859.97) * mm});
            skLineSegment(sketch, "E74.5.0.0", {"start": v(10664.83, 2859.97) * mm, "end": v(10596.83, 2895.97) * mm});
            skLineSegment(sketch, "E74.5.0.1", {"start": v(10596.83, 2895.97) * mm, "end": v(10524.83, 2895.97) * mm});
            skLineSegment(sketch, "E74.5.0.2", {"start": v(10524.83, 2895.97) * mm, "end": v(10456.83, 2859.97) * mm});
            skLineSegment(sketch, "E74.5.0.3", {"start": v(10456.83, 2859.97) * mm, "end": v(10386.83, 2859.97) * mm});
            skLineSegment(sketch, "E74.6.0.0", {"start": v(10386.83, 2859.97) * mm, "end": v(10318.83, 2895.97) * mm});
            skLineSegment(sketch, "E74.6.0.1", {"start": v(10318.83, 2895.97) * mm, "end": v(10246.83, 2895.97) * mm});
            skLineSegment(sketch, "E74.6.0.2", {"start": v(10246.83, 2895.97) * mm, "end": v(10178.83, 2859.97) * mm});
            skLineSegment(sketch, "E74.6.0.3", {"start": v(10178.83, 2859.97) * mm, "end": v(10108.83, 2859.97) * mm});
            skLineSegment(sketch, "E74.direction1", {"start": v(12054.83, 2859.97) * mm, "end": v(11776.83, 2859.97) * mm, "construction": true});
            skLineSegment(sketch, "E75.1.0.0", {"start": v(10108.83, 2859.97) * mm, "end": v(10040.83, 2895.97) * mm});
            skLineSegment(sketch, "E75.1.0.1", {"start": v(10040.83, 2895.97) * mm, "end": v(9968.83, 2895.97) * mm});
            skLineSegment(sketch, "E75.1.0.2", {"start": v(9968.83, 2895.97) * mm, "end": v(9900.83, 2859.97) * mm});
            skLineSegment(sketch, "E75.direction1", {"start": v(10386.83, 2859.97) * mm, "end": v(10108.83, 2859.97) * mm, "construction": true});
            skLineSegment(sketch, "E76.0.1.0", {"start": v(12054.83, 2858.97) * mm, "end": v(11776.83, 2858.97) * mm, "construction": true});
            skLineSegment(sketch, "E76.0.1.1", {"start": v(10386.83, 2858.97) * mm, "end": v(10108.83, 2858.97) * mm, "construction": true});
            skLineSegment(sketch, "E76.0.1.2", {"start": v(10108.83, 2858.97) * mm, "end": v(10040.83, 2894.97) * mm});
            skLineSegment(sketch, "E76.0.1.3", {"start": v(11012.83, 2858.97) * mm, "end": v(10942.83, 2858.97) * mm});
            skLineSegment(sketch, "E76.0.1.5", {"start": v(11358.83, 2894.97) * mm, "end": v(11290.83, 2858.97) * mm});
            skLineSegment(sketch, "E76.0.1.6", {"start": v(11220.83, 2858.97) * mm, "end": v(11152.83, 2894.97) * mm});
            skLineSegment(sketch, "E76.0.1.7", {"start": v(10802.83, 2894.97) * mm, "end": v(10734.83, 2858.97) * mm});
            skLineSegment(sketch, "E76.0.1.8", {"start": v(10386.83, 2858.97) * mm, "end": v(10318.83, 2894.97) * mm});
            skLineSegment(sketch, "E76.0.1.9", {"start": v(11708.83, 2894.97) * mm, "end": v(11636.83, 2894.97) * mm});
            skLineSegment(sketch, "E76.0.1.10", {"start": v(9968.83, 2894.97) * mm, "end": v(9900.83, 2858.97) * mm});
            skLineSegment(sketch, "E76.0.1.11", {"start": v(10664.83, 2858.97) * mm, "end": v(10596.83, 2894.97) * mm});
            skLineSegment(sketch, "E76.0.1.12", {"start": v(11636.83, 2894.97) * mm, "end": v(11568.83, 2858.97) * mm});
            skLineSegment(sketch, "E76.0.1.13", {"start": v(11776.83, 2858.97) * mm, "end": v(11708.83, 2894.97) * mm});
            skLineSegment(sketch, "E76.0.1.14", {"start": v(10246.83, 2894.97) * mm, "end": v(10178.83, 2858.97) * mm});
            skLineSegment(sketch, "E76.0.1.15", {"start": v(11430.83, 2894.97) * mm, "end": v(11358.83, 2894.97) * mm});
            skLineSegment(sketch, "E76.0.1.16", {"start": v(10942.83, 2858.97) * mm, "end": v(10874.83, 2894.97) * mm});
            skLineSegment(sketch, "E76.0.1.17", {"start": v(11498.83, 2858.97) * mm, "end": v(11430.83, 2894.97) * mm});
            skLineSegment(sketch, "E76.0.1.18", {"start": v(10040.83, 2894.97) * mm, "end": v(9968.83, 2894.97) * mm});
            skLineSegment(sketch, "E76.0.1.19", {"start": v(10734.83, 2858.97) * mm, "end": v(10664.83, 2858.97) * mm});
            skLineSegment(sketch, "E76.0.1.20", {"start": v(10596.83, 2894.97) * mm, "end": v(10524.83, 2894.97) * mm});
            skLineSegment(sketch, "E76.0.1.21", {"start": v(10524.83, 2894.97) * mm, "end": v(10456.83, 2858.97) * mm});
            skLineSegment(sketch, "E76.0.1.22", {"start": v(11568.83, 2858.97) * mm, "end": v(11498.83, 2858.97) * mm});
            skLineSegment(sketch, "E76.0.1.23", {"start": v(10318.83, 2894.97) * mm, "end": v(10246.83, 2894.97) * mm});
            skLineSegment(sketch, "E76.0.1.24", {"start": v(11914.83, 2894.97) * mm, "end": v(11846.83, 2858.97) * mm});
            skLineSegment(sketch, "E76.0.1.25", {"start": v(10874.83, 2894.97) * mm, "end": v(10802.83, 2894.97) * mm});
            skLineSegment(sketch, "E76.0.1.26", {"start": v(12054.83, 2858.97) * mm, "end": v(11986.83, 2894.97) * mm});
            skLineSegment(sketch, "E76.0.1.27", {"start": v(11290.83, 2858.97) * mm, "end": v(11220.83, 2858.97) * mm});
            skLineSegment(sketch, "E76.0.1.28", {"start": v(11152.83, 2894.97) * mm, "end": v(11080.83, 2894.97) * mm});
            skLineSegment(sketch, "E76.0.1.29", {"start": v(11986.83, 2894.97) * mm, "end": v(11914.83, 2894.97) * mm});
            skLineSegment(sketch, "E76.0.1.30", {"start": v(11080.83, 2894.97) * mm, "end": v(11012.83, 2858.97) * mm});
            skLineSegment(sketch, "E76.0.1.31", {"start": v(10178.83, 2858.97) * mm, "end": v(10108.83, 2858.97) * mm});
            skLineSegment(sketch, "E76.0.1.32", {"start": v(11846.83, 2858.97) * mm, "end": v(11776.83, 2858.97) * mm});
            skLineSegment(sketch, "E76.0.1.33", {"start": v(10456.83, 2858.97) * mm, "end": v(10386.83, 2858.97) * mm});
            skLineSegment(sketch, "E76.0.1.34", {"start": v(12091.83, 2858.97) * mm, "end": v(12054.83, 2858.97) * mm});
            skLineSegment(sketch, "E77", {"start": v(12091.83, 2858.97) * mm, "end": v(12092, 2858.97) * mm});
            skLineSegment(sketch, "E78", {"start": v(12092, 2858.97) * mm, "end": v(12092, 2859.97) * mm});
            skLineSegment(sketch, "E79", {"start": v(12092, 2859.97) * mm, "end": v(12091.83, 2859.97) * mm});
            skLineSegment(sketch, "E80.0.1.0", {"start": v(9412.83, 2895.97) * mm, "end": v(9344.83, 2859.97) * mm});
            skLineSegment(sketch, "E80.0.1.1", {"start": v(9412.83, 2894.97) * mm, "end": v(9344.83, 2858.97) * mm});
            skLineSegment(sketch, "E80.0.1.2", {"start": v(9484.83, 2895.97) * mm, "end": v(9412.83, 2895.97) * mm});
            skLineSegment(sketch, "E80.0.1.3", {"start": v(9762.83, 2895.97) * mm, "end": v(9690.83, 2895.97) * mm});
            skLineSegment(sketch, "E80.0.1.4", {"start": v(9552.83, 2858.97) * mm, "end": v(9484.83, 2894.97) * mm});
            skLineSegment(sketch, "E80.0.1.5", {"start": v(9622.83, 2858.97) * mm, "end": v(9552.83, 2858.97) * mm});
            skLineSegment(sketch, "E80.0.1.6", {"start": v(9274.83, 2858.97) * mm, "end": v(9206.83, 2894.97) * mm});
            skLineSegment(sketch, "E80.0.1.7", {"start": v(9690.83, 2894.97) * mm, "end": v(9622.83, 2858.97) * mm});
            skLineSegment(sketch, "E80.0.1.8", {"start": v(9274.83, 2859.97) * mm, "end": v(9206.83, 2895.97) * mm});
            skLineSegment(sketch, "E80.0.1.9", {"start": v(9622.83, 2859.97) * mm, "end": v(9552.83, 2859.97) * mm});
            skLineSegment(sketch, "E80.0.1.10", {"start": v(9900.83, 2858.97) * mm, "end": v(9830.83, 2858.97) * mm});
            skLineSegment(sketch, "E80.0.1.11", {"start": v(9344.83, 2859.97) * mm, "end": v(9274.83, 2859.97) * mm});
            skLineSegment(sketch, "E80.0.1.12", {"start": v(9484.83, 2894.97) * mm, "end": v(9412.83, 2894.97) * mm});
            skLineSegment(sketch, "E80.0.1.13", {"start": v(9830.83, 2858.97) * mm, "end": v(9762.83, 2894.97) * mm});
            skLineSegment(sketch, "E80.0.1.14", {"start": v(9830.83, 2859.97) * mm, "end": v(9762.83, 2895.97) * mm});
            skLineSegment(sketch, "E80.0.1.15", {"start": v(9206.83, 2895.97) * mm, "end": v(9134.83, 2895.97) * mm});
            skLineSegment(sketch, "E80.0.1.16", {"start": v(9690.83, 2895.97) * mm, "end": v(9622.83, 2859.97) * mm});
            skLineSegment(sketch, "E80.0.1.17", {"start": v(9900.83, 2859.97) * mm, "end": v(9830.83, 2859.97) * mm});
            skLineSegment(sketch, "E80.0.1.18", {"start": v(9762.83, 2894.97) * mm, "end": v(9690.83, 2894.97) * mm});
            skLineSegment(sketch, "E80.0.1.19", {"start": v(9552.83, 2859.97) * mm, "end": v(9484.83, 2895.97) * mm});
            skLineSegment(sketch, "E80.0.1.20", {"start": v(9206.83, 2894.97) * mm, "end": v(9134.83, 2894.97) * mm});
            skLineSegment(sketch, "E80.0.1.21", {"start": v(9344.83, 2858.97) * mm, "end": v(9274.83, 2858.97) * mm});
            skLineSegment(sketch, "E80.0.1.22", {"start": v(8440.83, 2859.97) * mm, "end": v(8162.83, 2859.97) * mm, "construction": true});
            skLineSegment(sketch, "E80.0.1.23", {"start": v(8022.83, 2895.97) * mm, "end": v(7954.83, 2859.97) * mm});
            skLineSegment(sketch, "E80.0.1.24", {"start": v(8022.83, 2894.97) * mm, "end": v(7954.83, 2858.97) * mm});
            skLineSegment(sketch, "E80.0.1.25", {"start": v(8440.83, 2858.97) * mm, "end": v(8162.83, 2858.97) * mm, "construction": true});
            skLineSegment(sketch, "E80.0.1.26", {"start": v(8856.83, 2894.97) * mm, "end": v(8788.83, 2858.97) * mm});
            skLineSegment(sketch, "E80.0.1.27", {"start": v(8856.83, 2895.97) * mm, "end": v(8788.83, 2859.97) * mm});
            skLineSegment(sketch, "E80.0.1.28", {"start": v(8094.83, 2895.97) * mm, "end": v(8022.83, 2895.97) * mm});
            skLineSegment(sketch, "E80.0.1.29", {"start": v(8162.83, 2859.97) * mm, "end": v(8094.83, 2895.97) * mm});
            skLineSegment(sketch, "E80.0.1.30", {"start": v(8928.83, 2895.97) * mm, "end": v(8856.83, 2895.97) * mm});
            skLineSegment(sketch, "E80.0.1.31", {"start": v(8928.83, 2894.97) * mm, "end": v(8856.83, 2894.97) * mm});
            skLineSegment(sketch, "E80.0.1.32", {"start": v(8162.83, 2858.97) * mm, "end": v(8094.83, 2894.97) * mm});
            skLineSegment(sketch, "E80.0.1.33", {"start": v(8094.83, 2894.97) * mm, "end": v(8022.83, 2894.97) * mm});
            skLineSegment(sketch, "E80.0.1.34", {"start": v(8510.83, 2858.97) * mm, "end": v(8440.83, 2858.97) * mm});
            skLineSegment(sketch, "E80.0.1.35", {"start": v(8650.83, 2894.97) * mm, "end": v(8578.83, 2894.97) * mm});
            skLineSegment(sketch, "E80.0.1.36", {"start": v(9066.83, 2858.97) * mm, "end": v(8996.83, 2858.97) * mm});
            skLineSegment(sketch, "E80.0.1.37", {"start": v(8300.83, 2894.97) * mm, "end": v(8232.83, 2858.97) * mm});
            skLineSegment(sketch, "E80.0.1.38", {"start": v(8718.83, 2859.97) * mm, "end": v(8650.83, 2895.97) * mm});
            skLineSegment(sketch, "E80.0.1.39", {"start": v(8578.83, 2894.97) * mm, "end": v(8510.83, 2858.97) * mm});
            skLineSegment(sketch, "E80.0.1.40", {"start": v(8372.83, 2895.97) * mm, "end": v(8300.83, 2895.97) * mm});
            skLineSegment(sketch, "E80.0.1.41", {"start": v(8440.83, 2859.97) * mm, "end": v(8372.83, 2895.97) * mm});
            skLineSegment(sketch, "E80.0.1.42", {"start": v(8650.83, 2895.97) * mm, "end": v(8578.83, 2895.97) * mm});
            skLineSegment(sketch, "E80.0.1.43", {"start": v(9066.83, 2859.97) * mm, "end": v(8996.83, 2859.97) * mm});
            skLineSegment(sketch, "E80.0.1.44", {"start": v(8718.83, 2858.97) * mm, "end": v(8650.83, 2894.97) * mm});
            skLineSegment(sketch, "E80.0.1.45", {"start": v(8996.83, 2858.97) * mm, "end": v(8928.83, 2894.97) * mm});
            skLineSegment(sketch, "E80.0.1.46", {"start": v(9134.83, 2894.97) * mm, "end": v(9066.83, 2858.97) * mm});
            skLineSegment(sketch, "E80.0.1.47", {"start": v(8372.83, 2894.97) * mm, "end": v(8300.83, 2894.97) * mm});
            skLineSegment(sketch, "E80.0.1.48", {"start": v(8788.83, 2858.97) * mm, "end": v(8718.83, 2858.97) * mm});
            skLineSegment(sketch, "E80.0.1.49", {"start": v(8232.83, 2858.97) * mm, "end": v(8162.83, 2858.97) * mm});
            skLineSegment(sketch, "E80.0.1.50", {"start": v(8788.83, 2859.97) * mm, "end": v(8718.83, 2859.97) * mm});
            skLineSegment(sketch, "E80.0.1.51", {"start": v(9134.83, 2895.97) * mm, "end": v(9066.83, 2859.97) * mm});
            skLineSegment(sketch, "E80.0.1.52", {"start": v(8996.83, 2859.97) * mm, "end": v(8928.83, 2895.97) * mm});
            skLineSegment(sketch, "E80.0.1.53", {"start": v(8232.83, 2859.97) * mm, "end": v(8162.83, 2859.97) * mm});
            skLineSegment(sketch, "E80.0.1.54", {"start": v(8510.83, 2859.97) * mm, "end": v(8440.83, 2859.97) * mm});
            skLineSegment(sketch, "E80.0.1.55", {"start": v(8300.83, 2895.97) * mm, "end": v(8232.83, 2859.97) * mm});
            skLineSegment(sketch, "E80.0.1.56", {"start": v(8578.83, 2895.97) * mm, "end": v(8510.83, 2859.97) * mm});
            skLineSegment(sketch, "E80.0.1.57", {"start": v(8440.83, 2858.97) * mm, "end": v(8372.83, 2894.97) * mm});
            skLineSegment(sketch, "E80.0.2.0", {"start": v(7466.83, 2895.97) * mm, "end": v(7398.83, 2859.97) * mm});
            skLineSegment(sketch, "E80.0.2.1", {"start": v(7466.83, 2894.97) * mm, "end": v(7398.83, 2858.97) * mm});
            skLineSegment(sketch, "E80.0.2.2", {"start": v(7538.83, 2895.97) * mm, "end": v(7466.83, 2895.97) * mm});
            skLineSegment(sketch, "E80.0.2.3", {"start": v(7816.83, 2895.97) * mm, "end": v(7744.83, 2895.97) * mm});
            skLineSegment(sketch, "E80.0.2.4", {"start": v(7606.83, 2858.97) * mm, "end": v(7538.83, 2894.97) * mm});
            skLineSegment(sketch, "E80.0.2.5", {"start": v(7676.83, 2858.97) * mm, "end": v(7606.83, 2858.97) * mm});
            skLineSegment(sketch, "E80.0.2.6", {"start": v(7328.83, 2858.97) * mm, "end": v(7260.83, 2894.97) * mm});
            skLineSegment(sketch, "E80.0.2.7", {"start": v(7744.83, 2894.97) * mm, "end": v(7676.83, 2858.97) * mm});
            skLineSegment(sketch, "E80.0.2.8", {"start": v(7328.83, 2859.97) * mm, "end": v(7260.83, 2895.97) * mm});
            skLineSegment(sketch, "E80.0.2.9", {"start": v(7676.83, 2859.97) * mm, "end": v(7606.83, 2859.97) * mm});
            skLineSegment(sketch, "E80.0.2.10", {"start": v(7954.83, 2858.97) * mm, "end": v(7884.83, 2858.97) * mm});
            skLineSegment(sketch, "E80.0.2.11", {"start": v(7398.83, 2859.97) * mm, "end": v(7328.83, 2859.97) * mm});
            skLineSegment(sketch, "E80.0.2.12", {"start": v(7538.83, 2894.97) * mm, "end": v(7466.83, 2894.97) * mm});
            skLineSegment(sketch, "E80.0.2.13", {"start": v(7884.83, 2858.97) * mm, "end": v(7816.83, 2894.97) * mm});
            skLineSegment(sketch, "E80.0.2.14", {"start": v(7884.83, 2859.97) * mm, "end": v(7816.83, 2895.97) * mm});
            skLineSegment(sketch, "E80.0.2.15", {"start": v(7260.83, 2895.97) * mm, "end": v(7188.83, 2895.97) * mm});
            skLineSegment(sketch, "E80.0.2.16", {"start": v(7744.83, 2895.97) * mm, "end": v(7676.83, 2859.97) * mm});
            skLineSegment(sketch, "E80.0.2.17", {"start": v(7954.83, 2859.97) * mm, "end": v(7884.83, 2859.97) * mm});
            skLineSegment(sketch, "E80.0.2.18", {"start": v(7816.83, 2894.97) * mm, "end": v(7744.83, 2894.97) * mm});
            skLineSegment(sketch, "E80.0.2.19", {"start": v(7606.83, 2859.97) * mm, "end": v(7538.83, 2895.97) * mm});
            skLineSegment(sketch, "E80.0.2.20", {"start": v(7260.83, 2894.97) * mm, "end": v(7188.83, 2894.97) * mm});
            skLineSegment(sketch, "E80.0.2.21", {"start": v(7398.83, 2858.97) * mm, "end": v(7328.83, 2858.97) * mm});
            skLineSegment(sketch, "E80.0.2.22", {"start": v(6494.83, 2859.97) * mm, "end": v(6216.83, 2859.97) * mm, "construction": true});
            skLineSegment(sketch, "E80.0.2.23", {"start": v(6076.83, 2895.97) * mm, "end": v(6008.83, 2859.97) * mm});
            skLineSegment(sketch, "E80.0.2.24", {"start": v(6076.83, 2894.97) * mm, "end": v(6008.83, 2858.97) * mm});
            skLineSegment(sketch, "E80.0.2.25", {"start": v(6494.83, 2858.97) * mm, "end": v(6216.83, 2858.97) * mm, "construction": true});
            skLineSegment(sketch, "E80.0.2.26", {"start": v(6910.83, 2894.97) * mm, "end": v(6842.83, 2858.97) * mm});
            skLineSegment(sketch, "E80.0.2.27", {"start": v(6910.83, 2895.97) * mm, "end": v(6842.83, 2859.97) * mm});
            skLineSegment(sketch, "E80.0.2.28", {"start": v(6148.83, 2895.97) * mm, "end": v(6076.83, 2895.97) * mm});
            skLineSegment(sketch, "E80.0.2.29", {"start": v(6216.83, 2859.97) * mm, "end": v(6148.83, 2895.97) * mm});
            skLineSegment(sketch, "E80.0.2.30", {"start": v(6982.83, 2895.97) * mm, "end": v(6910.83, 2895.97) * mm});
            skLineSegment(sketch, "E80.0.2.31", {"start": v(6982.83, 2894.97) * mm, "end": v(6910.83, 2894.97) * mm});
            skLineSegment(sketch, "E80.0.2.32", {"start": v(6216.83, 2858.97) * mm, "end": v(6148.83, 2894.97) * mm});
            skLineSegment(sketch, "E80.0.2.33", {"start": v(6148.83, 2894.97) * mm, "end": v(6076.83, 2894.97) * mm});
            skLineSegment(sketch, "E80.0.2.34", {"start": v(6564.83, 2858.97) * mm, "end": v(6494.83, 2858.97) * mm});
            skLineSegment(sketch, "E80.0.2.35", {"start": v(6704.83, 2894.97) * mm, "end": v(6632.83, 2894.97) * mm});
            skLineSegment(sketch, "E80.0.2.36", {"start": v(7120.83, 2858.97) * mm, "end": v(7050.83, 2858.97) * mm});
            skLineSegment(sketch, "E80.0.2.37", {"start": v(6354.83, 2894.97) * mm, "end": v(6286.83, 2858.97) * mm});
            skLineSegment(sketch, "E80.0.2.38", {"start": v(6772.83, 2859.97) * mm, "end": v(6704.83, 2895.97) * mm});
            skLineSegment(sketch, "E80.0.2.39", {"start": v(6632.83, 2894.97) * mm, "end": v(6564.83, 2858.97) * mm});
            skLineSegment(sketch, "E80.0.2.40", {"start": v(6426.83, 2895.97) * mm, "end": v(6354.83, 2895.97) * mm});
            skLineSegment(sketch, "E80.0.2.41", {"start": v(6494.83, 2859.97) * mm, "end": v(6426.83, 2895.97) * mm});
            skLineSegment(sketch, "E80.0.2.42", {"start": v(6704.83, 2895.97) * mm, "end": v(6632.83, 2895.97) * mm});
            skLineSegment(sketch, "E80.0.2.43", {"start": v(7120.83, 2859.97) * mm, "end": v(7050.83, 2859.97) * mm});
            skLineSegment(sketch, "E80.0.2.44", {"start": v(6772.83, 2858.97) * mm, "end": v(6704.83, 2894.97) * mm});
            skLineSegment(sketch, "E80.0.2.45", {"start": v(7050.83, 2858.97) * mm, "end": v(6982.83, 2894.97) * mm});
            skLineSegment(sketch, "E80.0.2.46", {"start": v(7188.83, 2894.97) * mm, "end": v(7120.83, 2858.97) * mm});
            skLineSegment(sketch, "E80.0.2.47", {"start": v(6426.83, 2894.97) * mm, "end": v(6354.83, 2894.97) * mm});
            skLineSegment(sketch, "E80.0.2.48", {"start": v(6842.83, 2858.97) * mm, "end": v(6772.83, 2858.97) * mm});
            skLineSegment(sketch, "E80.0.2.49", {"start": v(6286.83, 2858.97) * mm, "end": v(6216.83, 2858.97) * mm});
            skLineSegment(sketch, "E80.0.2.50", {"start": v(6842.83, 2859.97) * mm, "end": v(6772.83, 2859.97) * mm});
            skLineSegment(sketch, "E80.0.2.51", {"start": v(7188.83, 2895.97) * mm, "end": v(7120.83, 2859.97) * mm});
            skLineSegment(sketch, "E80.0.2.52", {"start": v(7050.83, 2859.97) * mm, "end": v(6982.83, 2895.97) * mm});
            skLineSegment(sketch, "E80.0.2.53", {"start": v(6286.83, 2859.97) * mm, "end": v(6216.83, 2859.97) * mm});
            skLineSegment(sketch, "E80.0.2.54", {"start": v(6564.83, 2859.97) * mm, "end": v(6494.83, 2859.97) * mm});
            skLineSegment(sketch, "E80.0.2.55", {"start": v(6354.83, 2895.97) * mm, "end": v(6286.83, 2859.97) * mm});
            skLineSegment(sketch, "E80.0.2.56", {"start": v(6632.83, 2895.97) * mm, "end": v(6564.83, 2859.97) * mm});
            skLineSegment(sketch, "E80.0.2.57", {"start": v(6494.83, 2858.97) * mm, "end": v(6426.83, 2894.97) * mm});
            skLineSegment(sketch, "E80.0.3.0", {"start": v(5520.83, 2895.97) * mm, "end": v(5452.83, 2859.97) * mm});
            skLineSegment(sketch, "E80.0.3.1", {"start": v(5520.83, 2894.97) * mm, "end": v(5452.83, 2858.97) * mm});
            skLineSegment(sketch, "E80.0.3.2", {"start": v(5592.83, 2895.97) * mm, "end": v(5520.83, 2895.97) * mm});
            skLineSegment(sketch, "E80.0.3.3", {"start": v(5870.83, 2895.97) * mm, "end": v(5798.83, 2895.97) * mm});
            skLineSegment(sketch, "E80.0.3.4", {"start": v(5660.83, 2858.97) * mm, "end": v(5592.83, 2894.97) * mm});
            skLineSegment(sketch, "E80.0.3.5", {"start": v(5730.83, 2858.97) * mm, "end": v(5660.83, 2858.97) * mm});
            skLineSegment(sketch, "E80.0.3.6", {"start": v(5382.83, 2858.97) * mm, "end": v(5314.83, 2894.97) * mm});
            skLineSegment(sketch, "E80.0.3.7", {"start": v(5798.83, 2894.97) * mm, "end": v(5730.83, 2858.97) * mm});
            skLineSegment(sketch, "E80.0.3.8", {"start": v(5382.83, 2859.97) * mm, "end": v(5314.83, 2895.97) * mm});
            skLineSegment(sketch, "E80.0.3.9", {"start": v(5730.83, 2859.97) * mm, "end": v(5660.83, 2859.97) * mm});
            skLineSegment(sketch, "E80.0.3.10", {"start": v(6008.83, 2858.97) * mm, "end": v(5938.83, 2858.97) * mm});
            skLineSegment(sketch, "E80.0.3.11", {"start": v(5452.83, 2859.97) * mm, "end": v(5382.83, 2859.97) * mm});
            skLineSegment(sketch, "E80.0.3.12", {"start": v(5592.83, 2894.97) * mm, "end": v(5520.83, 2894.97) * mm});
            skLineSegment(sketch, "E80.0.3.13", {"start": v(5938.83, 2858.97) * mm, "end": v(5870.83, 2894.97) * mm});
            skLineSegment(sketch, "E80.0.3.14", {"start": v(5938.83, 2859.97) * mm, "end": v(5870.83, 2895.97) * mm});
            skLineSegment(sketch, "E80.0.3.15", {"start": v(5314.83, 2895.97) * mm, "end": v(5242.83, 2895.97) * mm});
            skLineSegment(sketch, "E80.0.3.16", {"start": v(5798.83, 2895.97) * mm, "end": v(5730.83, 2859.97) * mm});
            skLineSegment(sketch, "E80.0.3.17", {"start": v(6008.83, 2859.97) * mm, "end": v(5938.83, 2859.97) * mm});
            skLineSegment(sketch, "E80.0.3.18", {"start": v(5870.83, 2894.97) * mm, "end": v(5798.83, 2894.97) * mm});
            skLineSegment(sketch, "E80.0.3.19", {"start": v(5660.83, 2859.97) * mm, "end": v(5592.83, 2895.97) * mm});
            skLineSegment(sketch, "E80.0.3.20", {"start": v(5314.83, 2894.97) * mm, "end": v(5242.83, 2894.97) * mm});
            skLineSegment(sketch, "E80.0.3.21", {"start": v(5452.83, 2858.97) * mm, "end": v(5382.83, 2858.97) * mm});
            skLineSegment(sketch, "E80.0.3.22", {"start": v(4548.83, 2859.97) * mm, "end": v(4270.83, 2859.97) * mm, "construction": true});
            skLineSegment(sketch, "E80.0.3.23", {"start": v(4130.83, 2895.97) * mm, "end": v(4062.83, 2859.97) * mm});
            skLineSegment(sketch, "E80.0.3.24", {"start": v(4130.83, 2894.97) * mm, "end": v(4062.83, 2858.97) * mm});
            skLineSegment(sketch, "E80.0.3.25", {"start": v(4548.83, 2858.97) * mm, "end": v(4270.83, 2858.97) * mm, "construction": true});
            skLineSegment(sketch, "E80.0.3.26", {"start": v(4964.83, 2894.97) * mm, "end": v(4896.83, 2858.97) * mm});
            skLineSegment(sketch, "E80.0.3.27", {"start": v(4964.83, 2895.97) * mm, "end": v(4896.83, 2859.97) * mm});
            skLineSegment(sketch, "E80.0.3.28", {"start": v(4202.83, 2895.97) * mm, "end": v(4130.83, 2895.97) * mm});
            skLineSegment(sketch, "E80.0.3.29", {"start": v(4270.83, 2859.97) * mm, "end": v(4202.83, 2895.97) * mm});
            skLineSegment(sketch, "E80.0.3.30", {"start": v(5036.83, 2895.97) * mm, "end": v(4964.83, 2895.97) * mm});
            skLineSegment(sketch, "E80.0.3.31", {"start": v(5036.83, 2894.97) * mm, "end": v(4964.83, 2894.97) * mm});
            skLineSegment(sketch, "E80.0.3.32", {"start": v(4270.83, 2858.97) * mm, "end": v(4202.83, 2894.97) * mm});
            skLineSegment(sketch, "E80.0.3.33", {"start": v(4202.83, 2894.97) * mm, "end": v(4130.83, 2894.97) * mm});
            skLineSegment(sketch, "E80.0.3.34", {"start": v(4618.83, 2858.97) * mm, "end": v(4548.83, 2858.97) * mm});
            skLineSegment(sketch, "E80.0.3.35", {"start": v(4758.83, 2894.97) * mm, "end": v(4686.83, 2894.97) * mm});
            skLineSegment(sketch, "E80.0.3.36", {"start": v(5174.83, 2858.97) * mm, "end": v(5104.83, 2858.97) * mm});
            skLineSegment(sketch, "E80.0.3.37", {"start": v(4408.83, 2894.97) * mm, "end": v(4340.83, 2858.97) * mm});
            skLineSegment(sketch, "E80.0.3.38", {"start": v(4826.83, 2859.97) * mm, "end": v(4758.83, 2895.97) * mm});
            skLineSegment(sketch, "E80.0.3.39", {"start": v(4686.83, 2894.97) * mm, "end": v(4618.83, 2858.97) * mm});
            skLineSegment(sketch, "E80.0.3.40", {"start": v(4480.83, 2895.97) * mm, "end": v(4408.83, 2895.97) * mm});
            skLineSegment(sketch, "E80.0.3.41", {"start": v(4548.83, 2859.97) * mm, "end": v(4480.83, 2895.97) * mm});
            skLineSegment(sketch, "E80.0.3.42", {"start": v(4758.83, 2895.97) * mm, "end": v(4686.83, 2895.97) * mm});
            skLineSegment(sketch, "E80.0.3.43", {"start": v(5174.83, 2859.97) * mm, "end": v(5104.83, 2859.97) * mm});
            skLineSegment(sketch, "E80.0.3.44", {"start": v(4826.83, 2858.97) * mm, "end": v(4758.83, 2894.97) * mm});
            skLineSegment(sketch, "E80.0.3.45", {"start": v(5104.83, 2858.97) * mm, "end": v(5036.83, 2894.97) * mm});
            skLineSegment(sketch, "E80.0.3.46", {"start": v(5242.83, 2894.97) * mm, "end": v(5174.83, 2858.97) * mm});
            skLineSegment(sketch, "E80.0.3.47", {"start": v(4480.83, 2894.97) * mm, "end": v(4408.83, 2894.97) * mm});
            skLineSegment(sketch, "E80.0.3.48", {"start": v(4896.83, 2858.97) * mm, "end": v(4826.83, 2858.97) * mm});
            skLineSegment(sketch, "E80.0.3.49", {"start": v(4340.83, 2858.97) * mm, "end": v(4270.83, 2858.97) * mm});
            skLineSegment(sketch, "E80.0.3.50", {"start": v(4896.83, 2859.97) * mm, "end": v(4826.83, 2859.97) * mm});
            skLineSegment(sketch, "E80.0.3.51", {"start": v(5242.83, 2895.97) * mm, "end": v(5174.83, 2859.97) * mm});
            skLineSegment(sketch, "E80.0.3.52", {"start": v(5104.83, 2859.97) * mm, "end": v(5036.83, 2895.97) * mm});
            skLineSegment(sketch, "E80.0.3.53", {"start": v(4340.83, 2859.97) * mm, "end": v(4270.83, 2859.97) * mm});
            skLineSegment(sketch, "E80.0.3.54", {"start": v(4618.83, 2859.97) * mm, "end": v(4548.83, 2859.97) * mm});
            skLineSegment(sketch, "E80.0.3.55", {"start": v(4408.83, 2895.97) * mm, "end": v(4340.83, 2859.97) * mm});
            skLineSegment(sketch, "E80.0.3.56", {"start": v(4686.83, 2895.97) * mm, "end": v(4618.83, 2859.97) * mm});
            skLineSegment(sketch, "E80.0.3.57", {"start": v(4548.83, 2858.97) * mm, "end": v(4480.83, 2894.97) * mm});
            skLineSegment(sketch, "E80.0.4.0", {"start": v(3574.83, 2895.97) * mm, "end": v(3506.83, 2859.97) * mm});
            skLineSegment(sketch, "E80.0.4.1", {"start": v(3574.83, 2894.97) * mm, "end": v(3506.83, 2858.97) * mm});
            skLineSegment(sketch, "E80.0.4.2", {"start": v(3646.83, 2895.97) * mm, "end": v(3574.83, 2895.97) * mm});
            skLineSegment(sketch, "E80.0.4.3", {"start": v(3924.83, 2895.97) * mm, "end": v(3852.83, 2895.97) * mm});
            skLineSegment(sketch, "E80.0.4.4", {"start": v(3714.83, 2858.97) * mm, "end": v(3646.83, 2894.97) * mm});
            skLineSegment(sketch, "E80.0.4.5", {"start": v(3784.83, 2858.97) * mm, "end": v(3714.83, 2858.97) * mm});
            skLineSegment(sketch, "E80.0.4.6", {"start": v(3436.83, 2858.97) * mm, "end": v(3368.83, 2894.97) * mm});
            skLineSegment(sketch, "E80.0.4.7", {"start": v(3852.83, 2894.97) * mm, "end": v(3784.83, 2858.97) * mm});
            skLineSegment(sketch, "E80.0.4.8", {"start": v(3436.83, 2859.97) * mm, "end": v(3368.83, 2895.97) * mm});
            skLineSegment(sketch, "E80.0.4.9", {"start": v(3784.83, 2859.97) * mm, "end": v(3714.83, 2859.97) * mm});
            skLineSegment(sketch, "E80.0.4.10", {"start": v(4062.83, 2858.97) * mm, "end": v(3992.83, 2858.97) * mm});
            skLineSegment(sketch, "E80.0.4.11", {"start": v(3506.83, 2859.97) * mm, "end": v(3436.83, 2859.97) * mm});
            skLineSegment(sketch, "E80.0.4.12", {"start": v(3646.83, 2894.97) * mm, "end": v(3574.83, 2894.97) * mm});
            skLineSegment(sketch, "E80.0.4.13", {"start": v(3992.83, 2858.97) * mm, "end": v(3924.83, 2894.97) * mm});
            skLineSegment(sketch, "E80.0.4.14", {"start": v(3992.83, 2859.97) * mm, "end": v(3924.83, 2895.97) * mm});
            skLineSegment(sketch, "E80.0.4.15", {"start": v(3368.83, 2895.97) * mm, "end": v(3296.83, 2895.97) * mm});
            skLineSegment(sketch, "E80.0.4.16", {"start": v(3852.83, 2895.97) * mm, "end": v(3784.83, 2859.97) * mm});
            skLineSegment(sketch, "E80.0.4.17", {"start": v(4062.83, 2859.97) * mm, "end": v(3992.83, 2859.97) * mm});
            skLineSegment(sketch, "E80.0.4.18", {"start": v(3924.83, 2894.97) * mm, "end": v(3852.83, 2894.97) * mm});
            skLineSegment(sketch, "E80.0.4.19", {"start": v(3714.83, 2859.97) * mm, "end": v(3646.83, 2895.97) * mm});
            skLineSegment(sketch, "E80.0.4.20", {"start": v(3368.83, 2894.97) * mm, "end": v(3296.83, 2894.97) * mm});
            skLineSegment(sketch, "E80.0.4.21", {"start": v(3506.83, 2858.97) * mm, "end": v(3436.83, 2858.97) * mm});
            skLineSegment(sketch, "E80.0.4.22", {"start": v(2602.83, 2859.97) * mm, "end": v(2324.83, 2859.97) * mm, "construction": true});
            skLineSegment(sketch, "E80.0.4.23", {"start": v(2184.83, 2895.97) * mm, "end": v(2116.83, 2859.97) * mm});
            skLineSegment(sketch, "E80.0.4.24", {"start": v(2184.83, 2894.97) * mm, "end": v(2116.83, 2858.97) * mm});
            skLineSegment(sketch, "E80.0.4.25", {"start": v(2602.83, 2858.97) * mm, "end": v(2324.83, 2858.97) * mm, "construction": true});
            skLineSegment(sketch, "E80.0.4.26", {"start": v(3018.83, 2894.97) * mm, "end": v(2950.83, 2858.97) * mm});
            skLineSegment(sketch, "E80.0.4.27", {"start": v(3018.83, 2895.97) * mm, "end": v(2950.83, 2859.97) * mm});
            skLineSegment(sketch, "E80.0.4.28", {"start": v(2256.83, 2895.97) * mm, "end": v(2184.83, 2895.97) * mm});
            skLineSegment(sketch, "E80.0.4.29", {"start": v(2324.83, 2859.97) * mm, "end": v(2256.83, 2895.97) * mm});
            skLineSegment(sketch, "E80.0.4.30", {"start": v(3090.83, 2895.97) * mm, "end": v(3018.83, 2895.97) * mm});
            skLineSegment(sketch, "E80.0.4.31", {"start": v(3090.83, 2894.97) * mm, "end": v(3018.83, 2894.97) * mm});
            skLineSegment(sketch, "E80.0.4.32", {"start": v(2324.83, 2858.97) * mm, "end": v(2256.83, 2894.97) * mm});
            skLineSegment(sketch, "E80.0.4.33", {"start": v(2256.83, 2894.97) * mm, "end": v(2184.83, 2894.97) * mm});
            skLineSegment(sketch, "E80.0.4.34", {"start": v(2672.83, 2858.97) * mm, "end": v(2602.83, 2858.97) * mm});
            skLineSegment(sketch, "E80.0.4.35", {"start": v(2812.83, 2894.97) * mm, "end": v(2740.83, 2894.97) * mm});
            skLineSegment(sketch, "E80.0.4.36", {"start": v(3228.83, 2858.97) * mm, "end": v(3158.83, 2858.97) * mm});
            skLineSegment(sketch, "E80.0.4.37", {"start": v(2462.83, 2894.97) * mm, "end": v(2394.83, 2858.97) * mm});
            skLineSegment(sketch, "E80.0.4.38", {"start": v(2880.83, 2859.97) * mm, "end": v(2812.83, 2895.97) * mm});
            skLineSegment(sketch, "E80.0.4.39", {"start": v(2740.83, 2894.97) * mm, "end": v(2672.83, 2858.97) * mm});
            skLineSegment(sketch, "E80.0.4.40", {"start": v(2534.83, 2895.97) * mm, "end": v(2462.83, 2895.97) * mm});
            skLineSegment(sketch, "E80.0.4.41", {"start": v(2602.83, 2859.97) * mm, "end": v(2534.83, 2895.97) * mm});
            skLineSegment(sketch, "E80.0.4.42", {"start": v(2812.83, 2895.97) * mm, "end": v(2740.83, 2895.97) * mm});
            skLineSegment(sketch, "E80.0.4.43", {"start": v(3228.83, 2859.97) * mm, "end": v(3158.83, 2859.97) * mm});
            skLineSegment(sketch, "E80.0.4.44", {"start": v(2880.83, 2858.97) * mm, "end": v(2812.83, 2894.97) * mm});
            skLineSegment(sketch, "E80.0.4.45", {"start": v(3158.83, 2858.97) * mm, "end": v(3090.83, 2894.97) * mm});
            skLineSegment(sketch, "E80.0.4.46", {"start": v(3296.83, 2894.97) * mm, "end": v(3228.83, 2858.97) * mm});
            skLineSegment(sketch, "E80.0.4.47", {"start": v(2534.83, 2894.97) * mm, "end": v(2462.83, 2894.97) * mm});
            skLineSegment(sketch, "E80.0.4.48", {"start": v(2950.83, 2858.97) * mm, "end": v(2880.83, 2858.97) * mm});
            skLineSegment(sketch, "E80.0.4.49", {"start": v(2394.83, 2858.97) * mm, "end": v(2324.83, 2858.97) * mm});
            skLineSegment(sketch, "E80.0.4.50", {"start": v(2950.83, 2859.97) * mm, "end": v(2880.83, 2859.97) * mm});
            skLineSegment(sketch, "E80.0.4.51", {"start": v(3296.83, 2895.97) * mm, "end": v(3228.83, 2859.97) * mm});
            skLineSegment(sketch, "E80.0.4.52", {"start": v(3158.83, 2859.97) * mm, "end": v(3090.83, 2895.97) * mm});
            skLineSegment(sketch, "E80.0.4.53", {"start": v(2394.83, 2859.97) * mm, "end": v(2324.83, 2859.97) * mm});
            skLineSegment(sketch, "E80.0.4.54", {"start": v(2672.83, 2859.97) * mm, "end": v(2602.83, 2859.97) * mm});
            skLineSegment(sketch, "E80.0.4.55", {"start": v(2462.83, 2895.97) * mm, "end": v(2394.83, 2859.97) * mm});
            skLineSegment(sketch, "E80.0.4.56", {"start": v(2740.83, 2895.97) * mm, "end": v(2672.83, 2859.97) * mm});
            skLineSegment(sketch, "E80.0.4.57", {"start": v(2602.83, 2858.97) * mm, "end": v(2534.83, 2894.97) * mm});
            skLineSegment(sketch, "E80.0.5.0", {"start": v(1628.83, 2895.97) * mm, "end": v(1560.83, 2859.97) * mm});
            skLineSegment(sketch, "E80.0.5.1", {"start": v(1628.83, 2894.97) * mm, "end": v(1560.83, 2858.97) * mm});
            skLineSegment(sketch, "E80.0.5.2", {"start": v(1700.83, 2895.97) * mm, "end": v(1628.83, 2895.97) * mm});
            skLineSegment(sketch, "E80.0.5.3", {"start": v(1978.83, 2895.97) * mm, "end": v(1906.83, 2895.97) * mm});
            skLineSegment(sketch, "E80.0.5.4", {"start": v(1768.83, 2858.97) * mm, "end": v(1700.83, 2894.97) * mm});
            skLineSegment(sketch, "E80.0.5.5", {"start": v(1838.83, 2858.97) * mm, "end": v(1768.83, 2858.97) * mm});
            skLineSegment(sketch, "E80.0.5.6", {"start": v(1490.83, 2858.97) * mm, "end": v(1422.83, 2894.97) * mm});
            skLineSegment(sketch, "E80.0.5.7", {"start": v(1906.83, 2894.97) * mm, "end": v(1838.83, 2858.97) * mm});
            skLineSegment(sketch, "E80.0.5.8", {"start": v(1490.83, 2859.97) * mm, "end": v(1422.83, 2895.97) * mm});
            skLineSegment(sketch, "E80.0.5.9", {"start": v(1838.83, 2859.97) * mm, "end": v(1768.83, 2859.97) * mm});
            skLineSegment(sketch, "E80.0.5.10", {"start": v(2116.83, 2858.97) * mm, "end": v(2046.83, 2858.97) * mm});
            skLineSegment(sketch, "E80.0.5.11", {"start": v(1560.83, 2859.97) * mm, "end": v(1490.83, 2859.97) * mm});
            skLineSegment(sketch, "E80.0.5.12", {"start": v(1700.83, 2894.97) * mm, "end": v(1628.83, 2894.97) * mm});
            skLineSegment(sketch, "E80.0.5.13", {"start": v(2046.83, 2858.97) * mm, "end": v(1978.83, 2894.97) * mm});
            skLineSegment(sketch, "E80.0.5.14", {"start": v(2046.83, 2859.97) * mm, "end": v(1978.83, 2895.97) * mm});
            skLineSegment(sketch, "E80.0.5.15", {"start": v(1422.83, 2895.97) * mm, "end": v(1350.83, 2895.97) * mm});
            skLineSegment(sketch, "E80.0.5.16", {"start": v(1906.83, 2895.97) * mm, "end": v(1838.83, 2859.97) * mm});
            skLineSegment(sketch, "E80.0.5.17", {"start": v(2116.83, 2859.97) * mm, "end": v(2046.83, 2859.97) * mm});
            skLineSegment(sketch, "E80.0.5.18", {"start": v(1978.83, 2894.97) * mm, "end": v(1906.83, 2894.97) * mm});
            skLineSegment(sketch, "E80.0.5.19", {"start": v(1768.83, 2859.97) * mm, "end": v(1700.83, 2895.97) * mm});
            skLineSegment(sketch, "E80.0.5.20", {"start": v(1422.83, 2894.97) * mm, "end": v(1350.83, 2894.97) * mm});
            skLineSegment(sketch, "E80.0.5.21", {"start": v(1560.83, 2858.97) * mm, "end": v(1490.83, 2858.97) * mm});
            skLineSegment(sketch, "E80.0.5.22", {"start": v(656.83, 2859.97) * mm, "end": v(378.83, 2859.97) * mm, "construction": true});
            skLineSegment(sketch, "E80.0.5.23", {"start": v(238.83, 2895.97) * mm, "end": v(170.83, 2859.97) * mm});
            skLineSegment(sketch, "E80.0.5.24", {"start": v(238.83, 2894.97) * mm, "end": v(170.83, 2858.97) * mm});
            skLineSegment(sketch, "E80.0.5.25", {"start": v(656.83, 2858.97) * mm, "end": v(378.83, 2858.97) * mm, "construction": true});
            skLineSegment(sketch, "E80.0.5.26", {"start": v(1072.83, 2894.97) * mm, "end": v(1004.83, 2858.97) * mm});
            skLineSegment(sketch, "E80.0.5.27", {"start": v(1072.83, 2895.97) * mm, "end": v(1004.83, 2859.97) * mm});
            skLineSegment(sketch, "E80.0.5.28", {"start": v(310.83, 2895.97) * mm, "end": v(238.83, 2895.97) * mm});
            skLineSegment(sketch, "E80.0.5.29", {"start": v(378.83, 2859.97) * mm, "end": v(310.83, 2895.97) * mm});
            skLineSegment(sketch, "E80.0.5.30", {"start": v(1144.83, 2895.97) * mm, "end": v(1072.83, 2895.97) * mm});
            skLineSegment(sketch, "E80.0.5.31", {"start": v(1144.83, 2894.97) * mm, "end": v(1072.83, 2894.97) * mm});
            skLineSegment(sketch, "E80.0.5.32", {"start": v(378.83, 2858.97) * mm, "end": v(310.83, 2894.97) * mm});
            skLineSegment(sketch, "E80.0.5.33", {"start": v(310.83, 2894.97) * mm, "end": v(238.83, 2894.97) * mm});
            skLineSegment(sketch, "E80.0.5.34", {"start": v(726.83, 2858.97) * mm, "end": v(656.83, 2858.97) * mm});
            skLineSegment(sketch, "E80.0.5.35", {"start": v(866.83, 2894.97) * mm, "end": v(794.83, 2894.97) * mm});
            skLineSegment(sketch, "E80.0.5.36", {"start": v(1282.83, 2858.97) * mm, "end": v(1212.83, 2858.97) * mm});
            skLineSegment(sketch, "E80.0.5.37", {"start": v(516.83, 2894.97) * mm, "end": v(448.83, 2858.97) * mm});
            skLineSegment(sketch, "E80.0.5.38", {"start": v(934.83, 2859.97) * mm, "end": v(866.83, 2895.97) * mm});
            skLineSegment(sketch, "E80.0.5.39", {"start": v(794.83, 2894.97) * mm, "end": v(726.83, 2858.97) * mm});
            skLineSegment(sketch, "E80.0.5.40", {"start": v(588.83, 2895.97) * mm, "end": v(516.83, 2895.97) * mm});
            skLineSegment(sketch, "E80.0.5.41", {"start": v(656.83, 2859.97) * mm, "end": v(588.83, 2895.97) * mm});
            skLineSegment(sketch, "E80.0.5.42", {"start": v(866.83, 2895.97) * mm, "end": v(794.83, 2895.97) * mm});
            skLineSegment(sketch, "E80.0.5.43", {"start": v(1282.83, 2859.97) * mm, "end": v(1212.83, 2859.97) * mm});
            skLineSegment(sketch, "E80.0.5.44", {"start": v(934.83, 2858.97) * mm, "end": v(866.83, 2894.97) * mm});
            skLineSegment(sketch, "E80.0.5.45", {"start": v(1212.83, 2858.97) * mm, "end": v(1144.83, 2894.97) * mm});
            skLineSegment(sketch, "E80.0.5.46", {"start": v(1350.83, 2894.97) * mm, "end": v(1282.83, 2858.97) * mm});
            skLineSegment(sketch, "E80.0.5.47", {"start": v(588.83, 2894.97) * mm, "end": v(516.83, 2894.97) * mm});
            skLineSegment(sketch, "E80.0.5.48", {"start": v(1004.83, 2858.97) * mm, "end": v(934.83, 2858.97) * mm});
            skLineSegment(sketch, "E80.0.5.49", {"start": v(448.83, 2858.97) * mm, "end": v(378.83, 2858.97) * mm});
            skLineSegment(sketch, "E80.0.5.50", {"start": v(1004.83, 2859.97) * mm, "end": v(934.83, 2859.97) * mm});
            skLineSegment(sketch, "E80.0.5.51", {"start": v(1350.83, 2895.97) * mm, "end": v(1282.83, 2859.97) * mm});
            skLineSegment(sketch, "E80.0.5.52", {"start": v(1212.83, 2859.97) * mm, "end": v(1144.83, 2895.97) * mm});
            skLineSegment(sketch, "E80.0.5.53", {"start": v(448.83, 2859.97) * mm, "end": v(378.83, 2859.97) * mm});
            skLineSegment(sketch, "E80.0.5.54", {"start": v(726.83, 2859.97) * mm, "end": v(656.83, 2859.97) * mm});
            skLineSegment(sketch, "E80.0.5.55", {"start": v(516.83, 2895.97) * mm, "end": v(448.83, 2859.97) * mm});
            skLineSegment(sketch, "E80.0.5.56", {"start": v(794.83, 2895.97) * mm, "end": v(726.83, 2859.97) * mm});
            skLineSegment(sketch, "E80.0.5.57", {"start": v(656.83, 2858.97) * mm, "end": v(588.83, 2894.97) * mm});
            skLineSegment(sketch, "E80.direction1", {"start": v(11846.83, 2858.97) * mm, "end": v(11846.83, 2883.97) * mm, "construction": true});
            skLineSegment(sketch, "E80.direction2", {"start": v(11846.83, 2858.97) * mm, "end": v(9900.83, 2858.97) * mm, "construction": true});
            skLineSegment(sketch, "E81", {"start": v(170.83, 2859.97) * mm, "end": v(100, 2859.97) * mm});
            skLineSegment(sketch, "E82", {"start": v(100, 2859.97) * mm, "end": v(100, 2858.97) * mm});
            skLineSegment(sketch, "E83", {"start": v(100, 2858.97) * mm, "end": v(170.83, 2858.97) * mm});
            skSolve(sketch);
        }
        {
            var Q0;
            Q0=qSketchRegion(id+"F16",true);
            extrude(context, id + "F17", {"entities" : qUnion([Q0]), "operationType" : NewBodyOperationType.ADD, "depth" : 2236 * mm, "offsetDistance" : 25 * mm});
        }
    });
